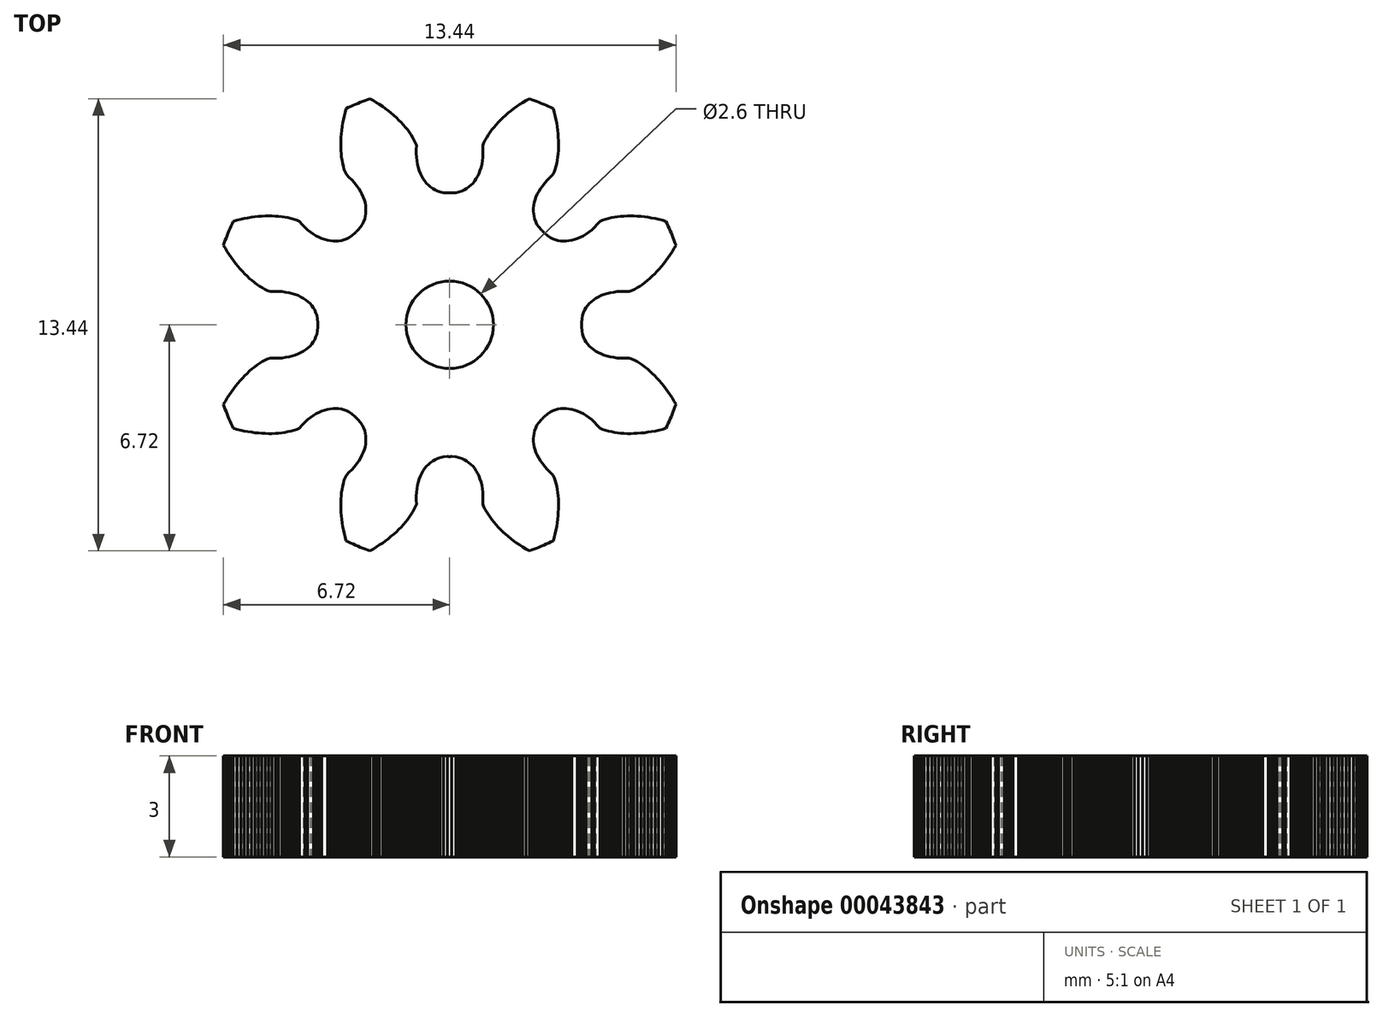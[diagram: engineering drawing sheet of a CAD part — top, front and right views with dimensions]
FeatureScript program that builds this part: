
annotation { "Feature Type Name" : "Feature", "Feature Type Description" : "" }
export const myFeature = defineFeature(function(context is Context, id is Id, definition is map)
    precondition{}
    {
        {
            var Q0;
            Q0=qCreatedBy(makeId("Top.planeOp"),FACE);
            var sketch = newSketch(context, id + "F0", { "sketchPlane" : qUnion([Q0])});
            skLineSegment(sketch, "E0", {"start": v(3.92, 0) * mm, "end": v(3.92, 0.01) * mm});
            skLineSegment(sketch, "E1", {"start": v(3.92, 0.01) * mm, "end": v(3.92, 0.03) * mm});
            skLineSegment(sketch, "E2", {"start": v(3.92, 0.03) * mm, "end": v(3.92, 0.04) * mm});
            skLineSegment(sketch, "E3", {"start": v(3.92, 0.04) * mm, "end": v(3.92, 0.05) * mm});
            skLineSegment(sketch, "E4", {"start": v(3.92, 0.05) * mm, "end": v(3.92, 0.06) * mm});
            skLineSegment(sketch, "E5", {"start": v(3.92, 0.06) * mm, "end": v(3.93, 0.18) * mm});
            skLineSegment(sketch, "E6", {"start": v(3.93, 0.18) * mm, "end": v(3.95, 0.28) * mm});
            skLineSegment(sketch, "E7", {"start": v(3.95, 0.28) * mm, "end": v(3.97, 0.36) * mm});
            skLineSegment(sketch, "E8", {"start": v(3.97, 0.36) * mm, "end": v(4, 0.44) * mm});
            skLineSegment(sketch, "E9", {"start": v(4, 0.44) * mm, "end": v(4.05, 0.5) * mm});
            skLineSegment(sketch, "E10", {"start": v(4.05, 0.5) * mm, "end": v(4.1, 0.57) * mm});
            skLineSegment(sketch, "E11", {"start": v(4.1, 0.57) * mm, "end": v(4.15, 0.63) * mm});
            skLineSegment(sketch, "E12", {"start": v(4.15, 0.63) * mm, "end": v(4.2, 0.69) * mm});
            skLineSegment(sketch, "E13", {"start": v(4.2, 0.69) * mm, "end": v(4.27, 0.74) * mm});
            skLineSegment(sketch, "E14", {"start": v(4.27, 0.74) * mm, "end": v(4.34, 0.79) * mm});
            skLineSegment(sketch, "E15", {"start": v(4.34, 0.79) * mm, "end": v(4.42, 0.83) * mm});
            skLineSegment(sketch, "E16", {"start": v(4.42, 0.83) * mm, "end": v(4.5, 0.87) * mm});
            skLineSegment(sketch, "E17", {"start": v(4.5, 0.87) * mm, "end": v(4.58, 0.9) * mm});
            skLineSegment(sketch, "E18", {"start": v(4.58, 0.9) * mm, "end": v(4.67, 0.93) * mm});
            skLineSegment(sketch, "E19", {"start": v(4.67, 0.93) * mm, "end": v(4.77, 0.96) * mm});
            skLineSegment(sketch, "E20", {"start": v(4.77, 0.96) * mm, "end": v(4.87, 0.97) * mm});
            skLineSegment(sketch, "E21", {"start": v(4.87, 0.97) * mm, "end": v(4.98, 0.99) * mm});
            skLineSegment(sketch, "E22", {"start": v(4.98, 0.99) * mm, "end": v(5.1, 1) * mm});
            skLineSegment(sketch, "E23", {"start": v(5.1, 1) * mm, "end": v(5.2, 0.99) * mm});
            skLineSegment(sketch, "E24", {"start": v(5.2, 0.99) * mm, "end": v(5.33, 0.99) * mm});
            skLineSegment(sketch, "E25", {"start": v(5.33, 0.99) * mm, "end": v(5.41, 1.02) * mm});
            skLineSegment(sketch, "E26", {"start": v(5.41, 1.02) * mm, "end": v(5.49, 1.06) * mm});
            skLineSegment(sketch, "E27", {"start": v(5.49, 1.06) * mm, "end": v(5.57, 1.1) * mm});
            skLineSegment(sketch, "E28", {"start": v(5.57, 1.1) * mm, "end": v(5.65, 1.15) * mm});
            skLineSegment(sketch, "E29", {"start": v(5.65, 1.15) * mm, "end": v(5.72, 1.2) * mm});
            skLineSegment(sketch, "E30", {"start": v(5.72, 1.2) * mm, "end": v(5.8, 1.25) * mm});
            skLineSegment(sketch, "E31", {"start": v(5.8, 1.25) * mm, "end": v(5.87, 1.31) * mm});
            skLineSegment(sketch, "E32", {"start": v(5.87, 1.31) * mm, "end": v(5.94, 1.38) * mm});
            skLineSegment(sketch, "E33", {"start": v(5.94, 1.38) * mm, "end": v(6.02, 1.44) * mm});
            skLineSegment(sketch, "E34", {"start": v(6.02, 1.44) * mm, "end": v(6.09, 1.51) * mm});
            skLineSegment(sketch, "E35", {"start": v(6.09, 1.51) * mm, "end": v(6.16, 1.58) * mm});
            skLineSegment(sketch, "E36", {"start": v(6.16, 1.58) * mm, "end": v(6.23, 1.66) * mm});
            skLineSegment(sketch, "E37", {"start": v(6.23, 1.66) * mm, "end": v(6.3, 1.74) * mm});
            skLineSegment(sketch, "E38", {"start": v(6.3, 1.74) * mm, "end": v(6.36, 1.82) * mm});
            skLineSegment(sketch, "E39", {"start": v(6.36, 1.82) * mm, "end": v(6.42, 1.9) * mm});
            skLineSegment(sketch, "E40", {"start": v(6.42, 1.9) * mm, "end": v(6.48, 2) * mm});
            skLineSegment(sketch, "E41", {"start": v(6.48, 2) * mm, "end": v(6.55, 2.08) * mm});
            skLineSegment(sketch, "E42", {"start": v(6.55, 2.08) * mm, "end": v(6.6, 2.17) * mm});
            skLineSegment(sketch, "E43", {"start": v(6.6, 2.17) * mm, "end": v(6.66, 2.27) * mm});
            skLineSegment(sketch, "E44", {"start": v(6.66, 2.27) * mm, "end": v(6.72, 2.37) * mm});
            skLineSegment(sketch, "E45", {"start": v(6.72, 2.37) * mm, "end": v(6.7, 2.44) * mm});
            skLineSegment(sketch, "E46", {"start": v(6.7, 2.44) * mm, "end": v(6.67, 2.51) * mm});
            skLineSegment(sketch, "E47", {"start": v(6.67, 2.51) * mm, "end": v(6.64, 2.58) * mm});
            skLineSegment(sketch, "E48", {"start": v(6.64, 2.58) * mm, "end": v(6.61, 2.66) * mm});
            skLineSegment(sketch, "E49", {"start": v(6.61, 2.66) * mm, "end": v(6.58, 2.73) * mm});
            skPoint(sketch, "E50", {"position": v(0, 5.7) * mm});
            skPoint(sketch, "E51", {"position": v(5.7, 0) * mm});
            skPoint(sketch, "E52", {"position": v(0, 0) * mm});
            skPoint(sketch, "E53", {"position": v(0, -5.7) * mm});
            skCircle(sketch, "E54", {"center": v(0, 0) * mm, "radius": 5.7 * mm, "construction": true});
            skLineSegment(sketch, "E55", {"start": v(5.7, 0) * mm, "end": v(-5.7, 0) * mm, "construction": true});
            skLineSegment(sketch, "E56", {"start": v(0, 5.7) * mm, "end": v(0, -5.7) * mm, "construction": true});
            skLineSegment(sketch, "E57.MirrorCS", {"start": v(3.92, 0) * mm, "end": v(3.92, -0.01) * mm});
            skLineSegment(sketch, "E58.MirrorCS", {"start": v(3.92, -0.03) * mm, "end": v(3.92, -0.04) * mm});
            skLineSegment(sketch, "E59.MirrorCS", {"start": v(3.92, -0.05) * mm, "end": v(3.92, -0.06) * mm});
            skLineSegment(sketch, "E60.MirrorCS", {"start": v(3.92, -0.01) * mm, "end": v(3.92, -0.03) * mm});
            skLineSegment(sketch, "E61.MirrorCS", {"start": v(3.92, -0.04) * mm, "end": v(3.92, -0.05) * mm});
            skLineSegment(sketch, "E62.MirrorCS", {"start": v(6.09, -1.51) * mm, "end": v(6.16, -1.58) * mm});
            skLineSegment(sketch, "E63.MirrorCS", {"start": v(4.67, -0.93) * mm, "end": v(4.77, -0.96) * mm});
            skLineSegment(sketch, "E64.MirrorCS", {"start": v(4.2, -0.69) * mm, "end": v(4.27, -0.74) * mm});
            skLineSegment(sketch, "E65.MirrorCS", {"start": v(4.27, -0.74) * mm, "end": v(4.34, -0.79) * mm});
            skLineSegment(sketch, "E66.MirrorCS", {"start": v(4.34, -0.79) * mm, "end": v(4.42, -0.83) * mm});
            skLineSegment(sketch, "E67.MirrorCS", {"start": v(3.92, -0.06) * mm, "end": v(3.93, -0.18) * mm});
            skLineSegment(sketch, "E68.MirrorCS", {"start": v(3.93, -0.18) * mm, "end": v(3.95, -0.28) * mm});
            skLineSegment(sketch, "E69.MirrorCS", {"start": v(3.95, -0.28) * mm, "end": v(3.97, -0.36) * mm});
            skLineSegment(sketch, "E70.MirrorCS", {"start": v(6.02, -1.44) * mm, "end": v(6.09, -1.51) * mm});
            skLineSegment(sketch, "E71.MirrorCS", {"start": v(3.97, -0.36) * mm, "end": v(4, -0.44) * mm});
            skLineSegment(sketch, "E72.MirrorCS", {"start": v(4, -0.44) * mm, "end": v(4.05, -0.5) * mm});
            skLineSegment(sketch, "E73.MirrorCS", {"start": v(4.05, -0.5) * mm, "end": v(4.1, -0.57) * mm});
            skLineSegment(sketch, "E74.MirrorCS", {"start": v(4.1, -0.57) * mm, "end": v(4.15, -0.63) * mm});
            skLineSegment(sketch, "E75.MirrorCS", {"start": v(4.15, -0.63) * mm, "end": v(4.2, -0.69) * mm});
            skLineSegment(sketch, "E76.MirrorCS", {"start": v(5.49, -1.06) * mm, "end": v(5.57, -1.1) * mm});
            skLineSegment(sketch, "E77.MirrorCS", {"start": v(6.6, -2.17) * mm, "end": v(6.66, -2.27) * mm});
            skLineSegment(sketch, "E78.MirrorCS", {"start": v(6.36, -1.82) * mm, "end": v(6.42, -1.9) * mm});
            skLineSegment(sketch, "E79.MirrorCS", {"start": v(5.1, -1) * mm, "end": v(5.2, -0.99) * mm});
            skLineSegment(sketch, "E80.MirrorCS", {"start": v(4.77, -0.96) * mm, "end": v(4.87, -0.97) * mm});
            skLineSegment(sketch, "E81.MirrorCS", {"start": v(6.72, -2.37) * mm, "end": v(6.7, -2.44) * mm});
            skLineSegment(sketch, "E82.MirrorCS", {"start": v(5.41, -1.02) * mm, "end": v(5.49, -1.06) * mm});
            skLineSegment(sketch, "E83.MirrorCS", {"start": v(5.65, -1.15) * mm, "end": v(5.72, -1.2) * mm});
            skLineSegment(sketch, "E84.MirrorCS", {"start": v(6.16, -1.58) * mm, "end": v(6.23, -1.66) * mm});
            skLineSegment(sketch, "E85.MirrorCS", {"start": v(4.42, -0.83) * mm, "end": v(4.5, -0.87) * mm});
            skLineSegment(sketch, "E86.MirrorCS", {"start": v(6.55, -2.08) * mm, "end": v(6.6, -2.17) * mm});
            skLineSegment(sketch, "E87.MirrorCS", {"start": v(6.64, -2.58) * mm, "end": v(6.61, -2.66) * mm});
            skLineSegment(sketch, "E88.MirrorCS", {"start": v(5.87, -1.31) * mm, "end": v(5.94, -1.38) * mm});
            skLineSegment(sketch, "E89.MirrorCS", {"start": v(6.66, -2.27) * mm, "end": v(6.72, -2.37) * mm});
            skLineSegment(sketch, "E90.MirrorCS", {"start": v(5.57, -1.1) * mm, "end": v(5.65, -1.15) * mm});
            skLineSegment(sketch, "E91.MirrorCS", {"start": v(6.42, -1.9) * mm, "end": v(6.48, -2) * mm});
            skLineSegment(sketch, "E92.MirrorCS", {"start": v(5.2, -0.99) * mm, "end": v(5.33, -0.99) * mm});
            skLineSegment(sketch, "E93.MirrorCS", {"start": v(4.87, -0.97) * mm, "end": v(4.98, -0.99) * mm});
            skLineSegment(sketch, "E94.MirrorCS", {"start": v(6.7, -2.44) * mm, "end": v(6.67, -2.51) * mm});
            skLineSegment(sketch, "E95.MirrorCS", {"start": v(5.72, -1.2) * mm, "end": v(5.8, -1.25) * mm});
            skLineSegment(sketch, "E96.MirrorCS", {"start": v(4.58, -0.9) * mm, "end": v(4.67, -0.93) * mm});
            skLineSegment(sketch, "E97.MirrorCS", {"start": v(6.23, -1.66) * mm, "end": v(6.3, -1.74) * mm});
            skLineSegment(sketch, "E98.MirrorCS", {"start": v(4.5, -0.87) * mm, "end": v(4.58, -0.9) * mm});
            skLineSegment(sketch, "E99.MirrorCS", {"start": v(6.61, -2.66) * mm, "end": v(6.58, -2.73) * mm});
            skLineSegment(sketch, "E100.MirrorCS", {"start": v(5.94, -1.38) * mm, "end": v(6.02, -1.44) * mm});
            skLineSegment(sketch, "E101.MirrorCS", {"start": v(6.48, -2) * mm, "end": v(6.55, -2.08) * mm});
            skLineSegment(sketch, "E102.MirrorCS", {"start": v(5.33, -0.99) * mm, "end": v(5.41, -1.02) * mm});
            skLineSegment(sketch, "E103.MirrorCS", {"start": v(6.67, -2.51) * mm, "end": v(6.64, -2.58) * mm});
            skLineSegment(sketch, "E104.MirrorCS", {"start": v(4.98, -0.99) * mm, "end": v(5.1, -1) * mm});
            skLineSegment(sketch, "E105.MirrorCS", {"start": v(6.3, -1.74) * mm, "end": v(6.36, -1.82) * mm});
            skLineSegment(sketch, "E106.MirrorCS", {"start": v(5.8, -1.25) * mm, "end": v(5.87, -1.31) * mm});
            skPoint(sketch, "E107.1.0", {"position": v(4.03, 4.03) * mm});
            skPoint(sketch, "E107.1.1", {"position": v(4.03, 4.03) * mm});
            skLineSegment(sketch, "E107.1.2", {"start": v(4.22, 2.82) * mm, "end": v(4.3, 2.9) * mm});
            skLineSegment(sketch, "E107.1.3", {"start": v(5.58, 3.23) * mm, "end": v(5.68, 3.22) * mm});
            skLineSegment(sketch, "E107.1.4", {"start": v(5.37, 3.23) * mm, "end": v(5.47, 3.23) * mm});
            skLineSegment(sketch, "E107.1.5", {"start": v(3.16, 6.1) * mm, "end": v(3.13, 6.2) * mm});
            skLineSegment(sketch, "E107.1.6", {"start": v(3.1, 4.54) * mm, "end": v(3.14, 4.63) * mm});
            skLineSegment(sketch, "E107.1.7", {"start": v(5.78, 3.2) * mm, "end": v(5.89, 3.2) * mm});
            skLineSegment(sketch, "E107.1.8", {"start": v(2.65, 3.96) * mm, "end": v(2.7, 4.05) * mm});
            skLineSegment(sketch, "E107.1.9", {"start": v(3.06, 2.56) * mm, "end": v(3.15, 2.52) * mm});
            skLineSegment(sketch, "E107.1.10", {"start": v(4.8, 3.18) * mm, "end": v(4.9, 3.2) * mm});
            skLineSegment(sketch, "E107.1.11", {"start": v(3.23, 5.37) * mm, "end": v(3.23, 5.47) * mm});
            skLineSegment(sketch, "E107.1.12", {"start": v(3.1, 6.32) * mm, "end": v(3.08, 6.43) * mm});
            skLineSegment(sketch, "E107.1.13", {"start": v(3.46, 2.49) * mm, "end": v(3.54, 2.5) * mm});
            skLineSegment(sketch, "E107.1.14", {"start": v(3.16, 4.71) * mm, "end": v(3.18, 4.8) * mm});
            skLineSegment(sketch, "E107.1.15", {"start": v(4.05, 2.7) * mm, "end": v(4.13, 2.76) * mm});
            skLineSegment(sketch, "E107.1.16", {"start": v(3.88, 2.6) * mm, "end": v(3.96, 2.65) * mm});
            skLineSegment(sketch, "E107.1.17", {"start": v(4.54, 3.1) * mm, "end": v(4.63, 3.14) * mm});
            skLineSegment(sketch, "E107.1.18", {"start": v(3.63, 2.51) * mm, "end": v(3.71, 2.54) * mm});
            skLineSegment(sketch, "E107.1.19", {"start": v(6.32, 3.1) * mm, "end": v(6.43, 3.08) * mm});
            skLineSegment(sketch, "E107.1.20", {"start": v(3.22, 2.5) * mm, "end": v(3.3, 2.5) * mm});
            skLineSegment(sketch, "E107.1.21", {"start": v(3.23, 5.58) * mm, "end": v(3.22, 5.68) * mm});
            skLineSegment(sketch, "E107.1.22", {"start": v(3.2, 4.9) * mm, "end": v(3.21, 4.99) * mm});
            skLineSegment(sketch, "E107.1.23", {"start": v(4.71, 3.16) * mm, "end": v(4.8, 3.18) * mm});
            skLineSegment(sketch, "E107.1.24", {"start": v(3.96, 2.65) * mm, "end": v(4.05, 2.7) * mm});
            skLineSegment(sketch, "E107.1.25", {"start": v(3.13, 6.2) * mm, "end": v(3.1, 6.32) * mm});
            skLineSegment(sketch, "E107.1.26", {"start": v(4.9, 3.2) * mm, "end": v(4.99, 3.21) * mm});
            skLineSegment(sketch, "E107.1.27", {"start": v(3.14, 4.63) * mm, "end": v(3.16, 4.71) * mm});
            skLineSegment(sketch, "E107.1.28", {"start": v(2.7, 4.05) * mm, "end": v(2.76, 4.13) * mm});
            skLineSegment(sketch, "E107.1.29", {"start": v(4.3, 2.9) * mm, "end": v(4.38, 2.98) * mm});
            skLineSegment(sketch, "E107.1.30", {"start": v(5.08, 3.22) * mm, "end": v(5.18, 3.23) * mm});
            skLineSegment(sketch, "E107.1.31", {"start": v(5.68, 3.22) * mm, "end": v(5.78, 3.2) * mm});
            skLineSegment(sketch, "E107.1.32", {"start": v(3.8, 2.57) * mm, "end": v(3.88, 2.6) * mm});
            skLineSegment(sketch, "E107.1.33", {"start": v(3.15, 2.52) * mm, "end": v(3.22, 2.5) * mm});
            skLineSegment(sketch, "E107.1.34", {"start": v(3.54, 2.5) * mm, "end": v(3.63, 2.51) * mm});
            skLineSegment(sketch, "E107.1.35", {"start": v(3.23, 5.47) * mm, "end": v(3.23, 5.58) * mm});
            skLineSegment(sketch, "E107.1.36", {"start": v(3.18, 4.8) * mm, "end": v(3.2, 4.9) * mm});
            skLineSegment(sketch, "E107.1.37", {"start": v(3.3, 2.5) * mm, "end": v(3.38, 2.49) * mm});
            skLineSegment(sketch, "E107.1.38", {"start": v(3.22, 5.68) * mm, "end": v(3.2, 5.78) * mm});
            skLineSegment(sketch, "E107.1.39", {"start": v(3.21, 4.99) * mm, "end": v(3.22, 5.08) * mm});
            skLineSegment(sketch, "E107.1.40", {"start": v(4.99, 3.21) * mm, "end": v(5.08, 3.22) * mm});
            skLineSegment(sketch, "E107.1.41", {"start": v(6.55, 2.8) * mm, "end": v(6.58, 2.73) * mm});
            skLineSegment(sketch, "E107.1.42", {"start": v(2.49, 3.46) * mm, "end": v(2.5, 3.54) * mm});
            skLineSegment(sketch, "E107.1.43", {"start": v(2.5, 3.54) * mm, "end": v(2.51, 3.63) * mm});
            skLineSegment(sketch, "E107.1.44", {"start": v(2.51, 3.63) * mm, "end": v(2.54, 3.71) * mm});
            skLineSegment(sketch, "E107.1.45", {"start": v(2.65, 2.9) * mm, "end": v(2.6, 2.99) * mm});
            skLineSegment(sketch, "E107.1.46", {"start": v(2.6, 2.99) * mm, "end": v(2.56, 3.06) * mm});
            skLineSegment(sketch, "E107.1.47", {"start": v(2.56, 3.06) * mm, "end": v(2.52, 3.15) * mm});
            skLineSegment(sketch, "E107.1.48", {"start": v(2.52, 3.15) * mm, "end": v(2.5, 3.22) * mm});
            skLineSegment(sketch, "E107.1.49", {"start": v(2.5, 3.22) * mm, "end": v(2.5, 3.3) * mm});
            skLineSegment(sketch, "E107.1.50", {"start": v(2.5, 3.3) * mm, "end": v(2.49, 3.38) * mm});
            skLineSegment(sketch, "E107.1.51", {"start": v(2.49, 3.38) * mm, "end": v(2.49, 3.46) * mm});
            skLineSegment(sketch, "E107.1.52", {"start": v(5.18, 3.23) * mm, "end": v(5.27, 3.23) * mm});
            skLineSegment(sketch, "E107.1.53", {"start": v(3.2, 5.78) * mm, "end": v(3.2, 5.89) * mm});
            skLineSegment(sketch, "E107.1.54", {"start": v(5.89, 3.2) * mm, "end": v(6, 3.18) * mm});
            skLineSegment(sketch, "E107.1.55", {"start": v(3.38, 2.49) * mm, "end": v(3.46, 2.49) * mm});
            skLineSegment(sketch, "E107.1.56", {"start": v(2.54, 3.71) * mm, "end": v(2.57, 3.8) * mm});
            skLineSegment(sketch, "E107.1.57", {"start": v(5.47, 3.23) * mm, "end": v(5.58, 3.23) * mm});
            skLineSegment(sketch, "E107.1.58", {"start": v(3.22, 5.08) * mm, "end": v(3.23, 5.18) * mm});
            skLineSegment(sketch, "E107.1.59", {"start": v(3.2, 5.89) * mm, "end": v(3.18, 6) * mm});
            skLineSegment(sketch, "E107.1.60", {"start": v(2.98, 4.38) * mm, "end": v(3.07, 4.47) * mm});
            skLineSegment(sketch, "E107.1.61", {"start": v(4.38, 2.98) * mm, "end": v(4.47, 3.07) * mm});
            skLineSegment(sketch, "E107.1.62", {"start": v(4.63, 3.14) * mm, "end": v(4.71, 3.16) * mm});
            skLineSegment(sketch, "E107.1.63", {"start": v(2.57, 3.8) * mm, "end": v(2.6, 3.88) * mm});
            skLineSegment(sketch, "E107.1.64", {"start": v(3.71, 2.54) * mm, "end": v(3.8, 2.57) * mm});
            skLineSegment(sketch, "E107.1.65", {"start": v(3.23, 5.18) * mm, "end": v(3.23, 5.27) * mm});
            skLineSegment(sketch, "E107.1.66", {"start": v(6, 3.18) * mm, "end": v(6.1, 3.16) * mm});
            skLineSegment(sketch, "E107.1.67", {"start": v(3.18, 6) * mm, "end": v(3.16, 6.1) * mm});
            skLineSegment(sketch, "E107.1.68", {"start": v(3.07, 4.47) * mm, "end": v(3.1, 4.54) * mm});
            skLineSegment(sketch, "E107.1.69", {"start": v(4.13, 2.76) * mm, "end": v(4.22, 2.82) * mm});
            skLineSegment(sketch, "E107.1.70", {"start": v(6.2, 3.13) * mm, "end": v(6.32, 3.1) * mm});
            skLineSegment(sketch, "E107.1.71", {"start": v(2.6, 3.88) * mm, "end": v(2.65, 3.96) * mm});
            skLineSegment(sketch, "E107.1.72", {"start": v(6.1, 3.16) * mm, "end": v(6.2, 3.13) * mm});
            skLineSegment(sketch, "E107.1.73", {"start": v(5.27, 3.23) * mm, "end": v(5.37, 3.23) * mm});
            skLineSegment(sketch, "E107.1.74", {"start": v(3.23, 5.27) * mm, "end": v(3.23, 5.37) * mm});
            skLineSegment(sketch, "E107.1.75", {"start": v(4.47, 3.07) * mm, "end": v(4.54, 3.1) * mm});
            skLineSegment(sketch, "E107.1.76", {"start": v(2.76, 4.13) * mm, "end": v(2.82, 4.22) * mm});
            skLineSegment(sketch, "E107.1.77", {"start": v(2.82, 4.22) * mm, "end": v(2.9, 4.3) * mm});
            skLineSegment(sketch, "E107.1.78", {"start": v(2.9, 4.3) * mm, "end": v(2.98, 4.38) * mm});
            skLineSegment(sketch, "E107.1.79", {"start": v(2.8, 6.55) * mm, "end": v(2.73, 6.58) * mm});
            skLineSegment(sketch, "E107.1.80", {"start": v(6.46, 3) * mm, "end": v(6.5, 2.94) * mm});
            skLineSegment(sketch, "E107.1.81", {"start": v(6.52, 2.87) * mm, "end": v(6.55, 2.8) * mm});
            skLineSegment(sketch, "E107.1.82", {"start": v(6.5, 2.94) * mm, "end": v(6.52, 2.87) * mm});
            skLineSegment(sketch, "E107.1.83", {"start": v(3, 6.46) * mm, "end": v(2.94, 6.5) * mm});
            skLineSegment(sketch, "E107.1.84", {"start": v(6.43, 3.08) * mm, "end": v(6.46, 3) * mm});
            skLineSegment(sketch, "E107.1.85", {"start": v(3.08, 6.43) * mm, "end": v(3, 6.46) * mm});
            skLineSegment(sketch, "E107.1.86", {"start": v(2.94, 6.5) * mm, "end": v(2.87, 6.52) * mm});
            skLineSegment(sketch, "E107.1.87", {"start": v(2.9, 2.65) * mm, "end": v(2.99, 2.6) * mm});
            skLineSegment(sketch, "E107.1.88", {"start": v(2.87, 6.52) * mm, "end": v(2.8, 6.55) * mm});
            skLineSegment(sketch, "E107.1.89", {"start": v(2.99, 2.6) * mm, "end": v(3.06, 2.56) * mm});
            skLineSegment(sketch, "E107.1.90", {"start": v(2.82, 2.73) * mm, "end": v(2.9, 2.65) * mm});
            skLineSegment(sketch, "E107.1.91", {"start": v(2.79, 2.75) * mm, "end": v(2.8, 2.74) * mm});
            skLineSegment(sketch, "E107.1.92", {"start": v(2.76, 2.78) * mm, "end": v(2.75, 2.79) * mm});
            skLineSegment(sketch, "E107.1.93", {"start": v(2.73, 2.82) * mm, "end": v(2.65, 2.9) * mm});
            skLineSegment(sketch, "E107.1.94", {"start": v(2.74, 2.8) * mm, "end": v(2.73, 2.82) * mm});
            skLineSegment(sketch, "E107.1.95", {"start": v(2.74, 2.8) * mm, "end": v(2.74, 2.8) * mm});
            skLineSegment(sketch, "E107.1.96", {"start": v(2.75, 2.79) * mm, "end": v(2.74, 2.8) * mm});
            skLineSegment(sketch, "E107.1.97", {"start": v(2.77, 2.77) * mm, "end": v(2.76, 2.78) * mm});
            skLineSegment(sketch, "E107.1.98", {"start": v(2.77, 2.77) * mm, "end": v(2.78, 2.76) * mm});
            skLineSegment(sketch, "E107.1.99", {"start": v(2.78, 2.76) * mm, "end": v(2.79, 2.75) * mm});
            skLineSegment(sketch, "E107.1.100", {"start": v(2.8, 2.74) * mm, "end": v(2.8, 2.74) * mm});
            skLineSegment(sketch, "E107.1.101", {"start": v(2.8, 2.74) * mm, "end": v(2.82, 2.73) * mm});
            skLineSegment(sketch, "E107.2.2", {"start": v(0.99, 4.98) * mm, "end": v(1, 5.1) * mm});
            skLineSegment(sketch, "E107.2.3", {"start": v(1.66, 6.23) * mm, "end": v(1.74, 6.3) * mm});
            skLineSegment(sketch, "E107.2.4", {"start": v(1.51, 6.09) * mm, "end": v(1.58, 6.16) * mm});
            skLineSegment(sketch, "E107.2.5", {"start": v(-2.08, 6.55) * mm, "end": v(-2.17, 6.6) * mm});
            skLineSegment(sketch, "E107.2.6", {"start": v(-1.02, 5.41) * mm, "end": v(-1.06, 5.49) * mm});
            skLineSegment(sketch, "E107.2.7", {"start": v(1.82, 6.36) * mm, "end": v(1.9, 6.42) * mm});
            skLineSegment(sketch, "E107.2.8", {"start": v(-0.93, 4.67) * mm, "end": v(-0.96, 4.77) * mm});
            skLineSegment(sketch, "E107.2.9", {"start": v(0.36, 3.97) * mm, "end": v(0.44, 4) * mm});
            skLineSegment(sketch, "E107.2.10", {"start": v(1.15, 5.65) * mm, "end": v(1.2, 5.72) * mm});
            skLineSegment(sketch, "E107.2.11", {"start": v(-1.51, 6.09) * mm, "end": v(-1.58, 6.16) * mm});
            skLineSegment(sketch, "E107.2.12", {"start": v(-2.27, 6.66) * mm, "end": v(-2.37, 6.72) * mm});
            skLineSegment(sketch, "E107.2.13", {"start": v(0.69, 4.2) * mm, "end": v(0.74, 4.27) * mm});
            skLineSegment(sketch, "E107.2.14", {"start": v(-1.1, 5.57) * mm, "end": v(-1.15, 5.65) * mm});
            skLineSegment(sketch, "E107.2.15", {"start": v(0.96, 4.77) * mm, "end": v(0.97, 4.87) * mm});
            skLineSegment(sketch, "E107.2.16", {"start": v(0.9, 4.58) * mm, "end": v(0.93, 4.67) * mm});
            skLineSegment(sketch, "E107.2.17", {"start": v(1.02, 5.41) * mm, "end": v(1.06, 5.49) * mm});
            skLineSegment(sketch, "E107.2.18", {"start": v(0.79, 4.34) * mm, "end": v(0.83, 4.42) * mm});
            skLineSegment(sketch, "E107.2.19", {"start": v(2.27, 6.66) * mm, "end": v(2.37, 6.72) * mm});
            skLineSegment(sketch, "E107.2.20", {"start": v(0.5, 4.05) * mm, "end": v(0.57, 4.1) * mm});
            skLineSegment(sketch, "E107.2.21", {"start": v(-1.66, 6.23) * mm, "end": v(-1.74, 6.3) * mm});
            skLineSegment(sketch, "E107.2.22", {"start": v(-1.2, 5.72) * mm, "end": v(-1.25, 5.8) * mm});
            skLineSegment(sketch, "E107.2.23", {"start": v(1.1, 5.57) * mm, "end": v(1.15, 5.65) * mm});
            skLineSegment(sketch, "E107.2.24", {"start": v(0.93, 4.67) * mm, "end": v(0.96, 4.77) * mm});
            skLineSegment(sketch, "E107.2.25", {"start": v(-2.17, 6.6) * mm, "end": v(-2.27, 6.66) * mm});
            skLineSegment(sketch, "E107.2.26", {"start": v(1.2, 5.72) * mm, "end": v(1.25, 5.8) * mm});
            skLineSegment(sketch, "E107.2.27", {"start": v(-1.06, 5.49) * mm, "end": v(-1.1, 5.57) * mm});
            skLineSegment(sketch, "E107.2.28", {"start": v(-0.96, 4.77) * mm, "end": v(-0.97, 4.87) * mm});
            skLineSegment(sketch, "E107.2.29", {"start": v(1, 5.1) * mm, "end": v(0.99, 5.2) * mm});
            skLineSegment(sketch, "E107.2.30", {"start": v(1.31, 5.87) * mm, "end": v(1.38, 5.94) * mm});
            skLineSegment(sketch, "E107.2.31", {"start": v(1.74, 6.3) * mm, "end": v(1.82, 6.36) * mm});
            skLineSegment(sketch, "E107.2.32", {"start": v(0.87, 4.5) * mm, "end": v(0.9, 4.58) * mm});
            skLineSegment(sketch, "E107.2.33", {"start": v(0.44, 4) * mm, "end": v(0.5, 4.05) * mm});
            skLineSegment(sketch, "E107.2.34", {"start": v(0.74, 4.27) * mm, "end": v(0.79, 4.34) * mm});
            skLineSegment(sketch, "E107.2.35", {"start": v(-1.58, 6.16) * mm, "end": v(-1.66, 6.23) * mm});
            skLineSegment(sketch, "E107.2.36", {"start": v(-1.15, 5.65) * mm, "end": v(-1.2, 5.72) * mm});
            skLineSegment(sketch, "E107.2.37", {"start": v(0.57, 4.1) * mm, "end": v(0.63, 4.15) * mm});
            skLineSegment(sketch, "E107.2.38", {"start": v(-1.74, 6.3) * mm, "end": v(-1.82, 6.36) * mm});
            skLineSegment(sketch, "E107.2.39", {"start": v(-1.25, 5.8) * mm, "end": v(-1.31, 5.87) * mm});
            skLineSegment(sketch, "E107.2.40", {"start": v(1.25, 5.8) * mm, "end": v(1.31, 5.87) * mm});
            skLineSegment(sketch, "E107.2.41", {"start": v(2.66, 6.61) * mm, "end": v(2.73, 6.58) * mm});
            skLineSegment(sketch, "E107.2.42", {"start": v(-0.69, 4.2) * mm, "end": v(-0.74, 4.27) * mm});
            skLineSegment(sketch, "E107.2.43", {"start": v(-0.74, 4.27) * mm, "end": v(-0.79, 4.34) * mm});
            skLineSegment(sketch, "E107.2.44", {"start": v(-0.79, 4.34) * mm, "end": v(-0.83, 4.42) * mm});
            skLineSegment(sketch, "E107.2.45", {"start": v(-0.18, 3.93) * mm, "end": v(-0.28, 3.95) * mm});
            skLineSegment(sketch, "E107.2.46", {"start": v(-0.28, 3.95) * mm, "end": v(-0.36, 3.97) * mm});
            skLineSegment(sketch, "E107.2.47", {"start": v(-0.36, 3.97) * mm, "end": v(-0.44, 4) * mm});
            skLineSegment(sketch, "E107.2.48", {"start": v(-0.44, 4) * mm, "end": v(-0.5, 4.05) * mm});
            skLineSegment(sketch, "E107.2.49", {"start": v(-0.5, 4.05) * mm, "end": v(-0.57, 4.1) * mm});
            skLineSegment(sketch, "E107.2.50", {"start": v(-0.57, 4.1) * mm, "end": v(-0.63, 4.15) * mm});
            skLineSegment(sketch, "E107.2.51", {"start": v(-0.63, 4.15) * mm, "end": v(-0.69, 4.2) * mm});
            skLineSegment(sketch, "E107.2.52", {"start": v(1.38, 5.94) * mm, "end": v(1.44, 6.02) * mm});
            skLineSegment(sketch, "E107.2.53", {"start": v(-1.82, 6.36) * mm, "end": v(-1.9, 6.42) * mm});
            skLineSegment(sketch, "E107.2.54", {"start": v(1.9, 6.42) * mm, "end": v(2, 6.48) * mm});
            skLineSegment(sketch, "E107.2.55", {"start": v(0.63, 4.15) * mm, "end": v(0.69, 4.2) * mm});
            skLineSegment(sketch, "E107.2.56", {"start": v(-0.83, 4.42) * mm, "end": v(-0.87, 4.5) * mm});
            skLineSegment(sketch, "E107.2.57", {"start": v(1.58, 6.16) * mm, "end": v(1.66, 6.23) * mm});
            skLineSegment(sketch, "E107.2.58", {"start": v(-1.31, 5.87) * mm, "end": v(-1.38, 5.94) * mm});
            skLineSegment(sketch, "E107.2.59", {"start": v(-1.9, 6.42) * mm, "end": v(-2, 6.48) * mm});
            skLineSegment(sketch, "E107.2.60", {"start": v(-0.99, 5.2) * mm, "end": v(-0.99, 5.33) * mm});
            skLineSegment(sketch, "E107.2.61", {"start": v(0.99, 5.2) * mm, "end": v(0.99, 5.33) * mm});
            skLineSegment(sketch, "E107.2.62", {"start": v(1.06, 5.49) * mm, "end": v(1.1, 5.57) * mm});
            skLineSegment(sketch, "E107.2.63", {"start": v(-0.87, 4.5) * mm, "end": v(-0.9, 4.58) * mm});
            skLineSegment(sketch, "E107.2.64", {"start": v(0.83, 4.42) * mm, "end": v(0.87, 4.5) * mm});
            skLineSegment(sketch, "E107.2.65", {"start": v(-1.38, 5.94) * mm, "end": v(-1.44, 6.02) * mm});
            skLineSegment(sketch, "E107.2.66", {"start": v(2, 6.48) * mm, "end": v(2.08, 6.55) * mm});
            skLineSegment(sketch, "E107.2.67", {"start": v(-2, 6.48) * mm, "end": v(-2.08, 6.55) * mm});
            skLineSegment(sketch, "E107.2.68", {"start": v(-0.99, 5.33) * mm, "end": v(-1.02, 5.41) * mm});
            skLineSegment(sketch, "E107.2.69", {"start": v(0.97, 4.87) * mm, "end": v(0.99, 4.98) * mm});
            skLineSegment(sketch, "E107.2.70", {"start": v(2.17, 6.6) * mm, "end": v(2.27, 6.66) * mm});
            skLineSegment(sketch, "E107.2.71", {"start": v(-0.9, 4.58) * mm, "end": v(-0.93, 4.67) * mm});
            skLineSegment(sketch, "E107.2.72", {"start": v(2.08, 6.55) * mm, "end": v(2.17, 6.6) * mm});
            skLineSegment(sketch, "E107.2.73", {"start": v(1.44, 6.02) * mm, "end": v(1.51, 6.09) * mm});
            skLineSegment(sketch, "E107.2.74", {"start": v(-1.44, 6.02) * mm, "end": v(-1.51, 6.09) * mm});
            skLineSegment(sketch, "E107.2.75", {"start": v(0.99, 5.33) * mm, "end": v(1.02, 5.41) * mm});
            skLineSegment(sketch, "E107.2.76", {"start": v(-0.97, 4.87) * mm, "end": v(-0.99, 4.98) * mm});
            skLineSegment(sketch, "E107.2.77", {"start": v(-0.99, 4.98) * mm, "end": v(-1, 5.1) * mm});
            skLineSegment(sketch, "E107.2.78", {"start": v(-1, 5.1) * mm, "end": v(-0.99, 5.2) * mm});
            skLineSegment(sketch, "E107.2.79", {"start": v(-2.66, 6.61) * mm, "end": v(-2.73, 6.58) * mm});
            skLineSegment(sketch, "E107.2.80", {"start": v(2.44, 6.7) * mm, "end": v(2.51, 6.67) * mm});
            skLineSegment(sketch, "E107.2.81", {"start": v(2.58, 6.64) * mm, "end": v(2.66, 6.61) * mm});
            skLineSegment(sketch, "E107.2.82", {"start": v(2.51, 6.67) * mm, "end": v(2.58, 6.64) * mm});
            skLineSegment(sketch, "E107.2.83", {"start": v(-2.44, 6.7) * mm, "end": v(-2.51, 6.67) * mm});
            skLineSegment(sketch, "E107.2.84", {"start": v(2.37, 6.72) * mm, "end": v(2.44, 6.7) * mm});
            skLineSegment(sketch, "E107.2.85", {"start": v(-2.37, 6.72) * mm, "end": v(-2.44, 6.7) * mm});
            skLineSegment(sketch, "E107.2.86", {"start": v(-2.51, 6.67) * mm, "end": v(-2.58, 6.64) * mm});
            skLineSegment(sketch, "E107.2.87", {"start": v(0.18, 3.93) * mm, "end": v(0.28, 3.95) * mm});
            skLineSegment(sketch, "E107.2.88", {"start": v(-2.58, 6.64) * mm, "end": v(-2.66, 6.61) * mm});
            skLineSegment(sketch, "E107.2.89", {"start": v(0.28, 3.95) * mm, "end": v(0.36, 3.97) * mm});
            skLineSegment(sketch, "E107.2.90", {"start": v(0.06, 3.92) * mm, "end": v(0.18, 3.93) * mm});
            skLineSegment(sketch, "E107.2.91", {"start": v(0.03, 3.92) * mm, "end": v(0.04, 3.92) * mm});
            skLineSegment(sketch, "E107.2.92", {"start": v(-0.01, 3.92) * mm, "end": v(-0.03, 3.92) * mm});
            skLineSegment(sketch, "E107.2.93", {"start": v(-0.06, 3.92) * mm, "end": v(-0.18, 3.93) * mm});
            skLineSegment(sketch, "E107.2.94", {"start": v(-0.05, 3.92) * mm, "end": v(-0.06, 3.92) * mm});
            skLineSegment(sketch, "E107.2.95", {"start": v(-0.04, 3.92) * mm, "end": v(-0.05, 3.92) * mm});
            skLineSegment(sketch, "E107.2.96", {"start": v(-0.03, 3.92) * mm, "end": v(-0.04, 3.92) * mm});
            skLineSegment(sketch, "E107.2.97", {"start": v(0, 3.92) * mm, "end": v(-0.01, 3.92) * mm});
            skLineSegment(sketch, "E107.2.98", {"start": v(0, 3.92) * mm, "end": v(0.01, 3.92) * mm});
            skLineSegment(sketch, "E107.2.99", {"start": v(0.01, 3.92) * mm, "end": v(0.03, 3.92) * mm});
            skLineSegment(sketch, "E107.2.100", {"start": v(0.04, 3.92) * mm, "end": v(0.05, 3.92) * mm});
            skLineSegment(sketch, "E107.2.101", {"start": v(0.05, 3.92) * mm, "end": v(0.06, 3.92) * mm});
            skPoint(sketch, "E107.3.0", {"position": v(-4.03, 4.03) * mm});
            skPoint(sketch, "E107.3.1", {"position": v(-4.03, 4.03) * mm});
            skLineSegment(sketch, "E107.3.2", {"start": v(-2.82, 4.22) * mm, "end": v(-2.9, 4.3) * mm});
            skLineSegment(sketch, "E107.3.3", {"start": v(-3.23, 5.58) * mm, "end": v(-3.22, 5.68) * mm});
            skLineSegment(sketch, "E107.3.4", {"start": v(-3.23, 5.37) * mm, "end": v(-3.23, 5.47) * mm});
            skLineSegment(sketch, "E107.3.5", {"start": v(-6.1, 3.16) * mm, "end": v(-6.2, 3.13) * mm});
            skLineSegment(sketch, "E107.3.6", {"start": v(-4.54, 3.1) * mm, "end": v(-4.63, 3.14) * mm});
            skLineSegment(sketch, "E107.3.7", {"start": v(-3.2, 5.78) * mm, "end": v(-3.2, 5.89) * mm});
            skLineSegment(sketch, "E107.3.8", {"start": v(-3.96, 2.65) * mm, "end": v(-4.05, 2.7) * mm});
            skLineSegment(sketch, "E107.3.9", {"start": v(-2.56, 3.06) * mm, "end": v(-2.52, 3.15) * mm});
            skLineSegment(sketch, "E107.3.10", {"start": v(-3.18, 4.8) * mm, "end": v(-3.2, 4.9) * mm});
            skLineSegment(sketch, "E107.3.11", {"start": v(-5.37, 3.23) * mm, "end": v(-5.47, 3.23) * mm});
            skLineSegment(sketch, "E107.3.12", {"start": v(-6.32, 3.1) * mm, "end": v(-6.43, 3.08) * mm});
            skLineSegment(sketch, "E107.3.13", {"start": v(-2.49, 3.46) * mm, "end": v(-2.5, 3.54) * mm});
            skLineSegment(sketch, "E107.3.14", {"start": v(-4.71, 3.16) * mm, "end": v(-4.8, 3.18) * mm});
            skLineSegment(sketch, "E107.3.15", {"start": v(-2.7, 4.05) * mm, "end": v(-2.76, 4.13) * mm});
            skLineSegment(sketch, "E107.3.16", {"start": v(-2.6, 3.88) * mm, "end": v(-2.65, 3.96) * mm});
            skLineSegment(sketch, "E107.3.17", {"start": v(-3.1, 4.54) * mm, "end": v(-3.14, 4.63) * mm});
            skLineSegment(sketch, "E107.3.18", {"start": v(-2.51, 3.63) * mm, "end": v(-2.54, 3.71) * mm});
            skLineSegment(sketch, "E107.3.19", {"start": v(-3.1, 6.32) * mm, "end": v(-3.08, 6.43) * mm});
            skLineSegment(sketch, "E107.3.20", {"start": v(-2.5, 3.22) * mm, "end": v(-2.5, 3.3) * mm});
            skLineSegment(sketch, "E107.3.21", {"start": v(-5.58, 3.23) * mm, "end": v(-5.68, 3.22) * mm});
            skLineSegment(sketch, "E107.3.22", {"start": v(-4.9, 3.2) * mm, "end": v(-4.99, 3.21) * mm});
            skLineSegment(sketch, "E107.3.23", {"start": v(-3.16, 4.71) * mm, "end": v(-3.18, 4.8) * mm});
            skLineSegment(sketch, "E107.3.24", {"start": v(-2.65, 3.96) * mm, "end": v(-2.7, 4.05) * mm});
            skLineSegment(sketch, "E107.3.25", {"start": v(-6.2, 3.13) * mm, "end": v(-6.32, 3.1) * mm});
            skLineSegment(sketch, "E107.3.26", {"start": v(-3.2, 4.9) * mm, "end": v(-3.21, 4.99) * mm});
            skLineSegment(sketch, "E107.3.27", {"start": v(-4.63, 3.14) * mm, "end": v(-4.71, 3.16) * mm});
            skLineSegment(sketch, "E107.3.28", {"start": v(-4.05, 2.7) * mm, "end": v(-4.13, 2.76) * mm});
            skLineSegment(sketch, "E107.3.29", {"start": v(-2.9, 4.3) * mm, "end": v(-2.98, 4.38) * mm});
            skLineSegment(sketch, "E107.3.30", {"start": v(-3.22, 5.08) * mm, "end": v(-3.23, 5.18) * mm});
            skLineSegment(sketch, "E107.3.31", {"start": v(-3.22, 5.68) * mm, "end": v(-3.2, 5.78) * mm});
            skLineSegment(sketch, "E107.3.32", {"start": v(-2.57, 3.8) * mm, "end": v(-2.6, 3.88) * mm});
            skLineSegment(sketch, "E107.3.33", {"start": v(-2.52, 3.15) * mm, "end": v(-2.5, 3.22) * mm});
            skLineSegment(sketch, "E107.3.34", {"start": v(-2.5, 3.54) * mm, "end": v(-2.51, 3.63) * mm});
            skLineSegment(sketch, "E107.3.35", {"start": v(-5.47, 3.23) * mm, "end": v(-5.58, 3.23) * mm});
            skLineSegment(sketch, "E107.3.36", {"start": v(-4.8, 3.18) * mm, "end": v(-4.9, 3.2) * mm});
            skLineSegment(sketch, "E107.3.37", {"start": v(-2.5, 3.3) * mm, "end": v(-2.49, 3.38) * mm});
            skLineSegment(sketch, "E107.3.38", {"start": v(-5.68, 3.22) * mm, "end": v(-5.78, 3.2) * mm});
            skLineSegment(sketch, "E107.3.39", {"start": v(-4.99, 3.21) * mm, "end": v(-5.08, 3.22) * mm});
            skLineSegment(sketch, "E107.3.40", {"start": v(-3.21, 4.99) * mm, "end": v(-3.22, 5.08) * mm});
            skLineSegment(sketch, "E107.3.41", {"start": v(-2.8, 6.55) * mm, "end": v(-2.73, 6.58) * mm});
            skLineSegment(sketch, "E107.3.42", {"start": v(-3.46, 2.49) * mm, "end": v(-3.54, 2.5) * mm});
            skLineSegment(sketch, "E107.3.43", {"start": v(-3.54, 2.5) * mm, "end": v(-3.63, 2.51) * mm});
            skLineSegment(sketch, "E107.3.44", {"start": v(-3.63, 2.51) * mm, "end": v(-3.71, 2.54) * mm});
            skLineSegment(sketch, "E107.3.45", {"start": v(-2.9, 2.65) * mm, "end": v(-2.99, 2.6) * mm});
            skLineSegment(sketch, "E107.3.46", {"start": v(-2.99, 2.6) * mm, "end": v(-3.06, 2.56) * mm});
            skLineSegment(sketch, "E107.3.47", {"start": v(-3.06, 2.56) * mm, "end": v(-3.15, 2.52) * mm});
            skLineSegment(sketch, "E107.3.48", {"start": v(-3.15, 2.52) * mm, "end": v(-3.22, 2.5) * mm});
            skLineSegment(sketch, "E107.3.49", {"start": v(-3.22, 2.5) * mm, "end": v(-3.3, 2.5) * mm});
            skLineSegment(sketch, "E107.3.50", {"start": v(-3.3, 2.5) * mm, "end": v(-3.38, 2.49) * mm});
            skLineSegment(sketch, "E107.3.51", {"start": v(-3.38, 2.49) * mm, "end": v(-3.46, 2.49) * mm});
            skLineSegment(sketch, "E107.3.52", {"start": v(-3.23, 5.18) * mm, "end": v(-3.23, 5.27) * mm});
            skLineSegment(sketch, "E107.3.53", {"start": v(-5.78, 3.2) * mm, "end": v(-5.89, 3.2) * mm});
            skLineSegment(sketch, "E107.3.54", {"start": v(-3.2, 5.89) * mm, "end": v(-3.18, 6) * mm});
            skLineSegment(sketch, "E107.3.55", {"start": v(-2.49, 3.38) * mm, "end": v(-2.49, 3.46) * mm});
            skLineSegment(sketch, "E107.3.56", {"start": v(-3.71, 2.54) * mm, "end": v(-3.8, 2.57) * mm});
            skLineSegment(sketch, "E107.3.57", {"start": v(-3.23, 5.47) * mm, "end": v(-3.23, 5.58) * mm});
            skLineSegment(sketch, "E107.3.58", {"start": v(-5.08, 3.22) * mm, "end": v(-5.18, 3.23) * mm});
            skLineSegment(sketch, "E107.3.59", {"start": v(-5.89, 3.2) * mm, "end": v(-6, 3.18) * mm});
            skLineSegment(sketch, "E107.3.60", {"start": v(-4.38, 2.98) * mm, "end": v(-4.47, 3.07) * mm});
            skLineSegment(sketch, "E107.3.61", {"start": v(-2.98, 4.38) * mm, "end": v(-3.07, 4.47) * mm});
            skLineSegment(sketch, "E107.3.62", {"start": v(-3.14, 4.63) * mm, "end": v(-3.16, 4.71) * mm});
            skLineSegment(sketch, "E107.3.63", {"start": v(-3.8, 2.57) * mm, "end": v(-3.88, 2.6) * mm});
            skLineSegment(sketch, "E107.3.64", {"start": v(-2.54, 3.71) * mm, "end": v(-2.57, 3.8) * mm});
            skLineSegment(sketch, "E107.3.65", {"start": v(-5.18, 3.23) * mm, "end": v(-5.27, 3.23) * mm});
            skLineSegment(sketch, "E107.3.66", {"start": v(-3.18, 6) * mm, "end": v(-3.16, 6.1) * mm});
            skLineSegment(sketch, "E107.3.67", {"start": v(-6, 3.18) * mm, "end": v(-6.1, 3.16) * mm});
            skLineSegment(sketch, "E107.3.68", {"start": v(-4.47, 3.07) * mm, "end": v(-4.54, 3.1) * mm});
            skLineSegment(sketch, "E107.3.69", {"start": v(-2.76, 4.13) * mm, "end": v(-2.82, 4.22) * mm});
            skLineSegment(sketch, "E107.3.70", {"start": v(-3.13, 6.2) * mm, "end": v(-3.1, 6.32) * mm});
            skLineSegment(sketch, "E107.3.71", {"start": v(-3.88, 2.6) * mm, "end": v(-3.96, 2.65) * mm});
            skLineSegment(sketch, "E107.3.72", {"start": v(-3.16, 6.1) * mm, "end": v(-3.13, 6.2) * mm});
            skLineSegment(sketch, "E107.3.73", {"start": v(-3.23, 5.27) * mm, "end": v(-3.23, 5.37) * mm});
            skLineSegment(sketch, "E107.3.74", {"start": v(-5.27, 3.23) * mm, "end": v(-5.37, 3.23) * mm});
            skLineSegment(sketch, "E107.3.75", {"start": v(-3.07, 4.47) * mm, "end": v(-3.1, 4.54) * mm});
            skLineSegment(sketch, "E107.3.76", {"start": v(-4.13, 2.76) * mm, "end": v(-4.22, 2.82) * mm});
            skLineSegment(sketch, "E107.3.77", {"start": v(-4.22, 2.82) * mm, "end": v(-4.3, 2.9) * mm});
            skLineSegment(sketch, "E107.3.78", {"start": v(-4.3, 2.9) * mm, "end": v(-4.38, 2.98) * mm});
            skLineSegment(sketch, "E107.3.79", {"start": v(-6.55, 2.8) * mm, "end": v(-6.58, 2.73) * mm});
            skLineSegment(sketch, "E107.3.80", {"start": v(-3, 6.46) * mm, "end": v(-2.94, 6.5) * mm});
            skLineSegment(sketch, "E107.3.81", {"start": v(-2.87, 6.52) * mm, "end": v(-2.8, 6.55) * mm});
            skLineSegment(sketch, "E107.3.82", {"start": v(-2.94, 6.5) * mm, "end": v(-2.87, 6.52) * mm});
            skLineSegment(sketch, "E107.3.83", {"start": v(-6.46, 3) * mm, "end": v(-6.5, 2.94) * mm});
            skLineSegment(sketch, "E107.3.84", {"start": v(-3.08, 6.43) * mm, "end": v(-3, 6.46) * mm});
            skLineSegment(sketch, "E107.3.85", {"start": v(-6.43, 3.08) * mm, "end": v(-6.46, 3) * mm});
            skLineSegment(sketch, "E107.3.86", {"start": v(-6.5, 2.94) * mm, "end": v(-6.52, 2.87) * mm});
            skLineSegment(sketch, "E107.3.87", {"start": v(-2.65, 2.9) * mm, "end": v(-2.6, 2.99) * mm});
            skLineSegment(sketch, "E107.3.88", {"start": v(-6.52, 2.87) * mm, "end": v(-6.55, 2.8) * mm});
            skLineSegment(sketch, "E107.3.89", {"start": v(-2.6, 2.99) * mm, "end": v(-2.56, 3.06) * mm});
            skLineSegment(sketch, "E107.3.90", {"start": v(-2.73, 2.82) * mm, "end": v(-2.65, 2.9) * mm});
            skLineSegment(sketch, "E107.3.91", {"start": v(-2.75, 2.79) * mm, "end": v(-2.74, 2.8) * mm});
            skLineSegment(sketch, "E107.3.92", {"start": v(-2.78, 2.76) * mm, "end": v(-2.79, 2.75) * mm});
            skLineSegment(sketch, "E107.3.93", {"start": v(-2.82, 2.73) * mm, "end": v(-2.9, 2.65) * mm});
            skLineSegment(sketch, "E107.3.94", {"start": v(-2.8, 2.74) * mm, "end": v(-2.82, 2.73) * mm});
            skLineSegment(sketch, "E107.3.95", {"start": v(-2.8, 2.74) * mm, "end": v(-2.8, 2.74) * mm});
            skLineSegment(sketch, "E107.3.96", {"start": v(-2.79, 2.75) * mm, "end": v(-2.8, 2.74) * mm});
            skLineSegment(sketch, "E107.3.97", {"start": v(-2.77, 2.77) * mm, "end": v(-2.78, 2.76) * mm});
            skLineSegment(sketch, "E107.3.98", {"start": v(-2.77, 2.77) * mm, "end": v(-2.76, 2.78) * mm});
            skLineSegment(sketch, "E107.3.99", {"start": v(-2.76, 2.78) * mm, "end": v(-2.75, 2.79) * mm});
            skLineSegment(sketch, "E107.3.100", {"start": v(-2.74, 2.8) * mm, "end": v(-2.74, 2.8) * mm});
            skLineSegment(sketch, "E107.3.101", {"start": v(-2.74, 2.8) * mm, "end": v(-2.73, 2.82) * mm});
            skPoint(sketch, "E107.4.0", {"position": v(-5.7, 0) * mm});
            skPoint(sketch, "E107.4.1", {"position": v(-5.7, 0) * mm});
            skLineSegment(sketch, "E107.4.2", {"start": v(-4.98, 0.99) * mm, "end": v(-5.1, 1) * mm});
            skLineSegment(sketch, "E107.4.3", {"start": v(-6.23, 1.66) * mm, "end": v(-6.3, 1.74) * mm});
            skLineSegment(sketch, "E107.4.4", {"start": v(-6.09, 1.51) * mm, "end": v(-6.16, 1.58) * mm});
            skLineSegment(sketch, "E107.4.5", {"start": v(-6.55, -2.08) * mm, "end": v(-6.6, -2.17) * mm});
            skLineSegment(sketch, "E107.4.6", {"start": v(-5.41, -1.02) * mm, "end": v(-5.49, -1.06) * mm});
            skLineSegment(sketch, "E107.4.7", {"start": v(-6.36, 1.82) * mm, "end": v(-6.42, 1.9) * mm});
            skLineSegment(sketch, "E107.4.8", {"start": v(-4.67, -0.93) * mm, "end": v(-4.77, -0.96) * mm});
            skLineSegment(sketch, "E107.4.9", {"start": v(-3.97, 0.36) * mm, "end": v(-4, 0.44) * mm});
            skLineSegment(sketch, "E107.4.10", {"start": v(-5.65, 1.15) * mm, "end": v(-5.72, 1.2) * mm});
            skLineSegment(sketch, "E107.4.11", {"start": v(-6.09, -1.51) * mm, "end": v(-6.16, -1.58) * mm});
            skLineSegment(sketch, "E107.4.12", {"start": v(-6.66, -2.27) * mm, "end": v(-6.72, -2.37) * mm});
            skLineSegment(sketch, "E107.4.13", {"start": v(-4.2, 0.69) * mm, "end": v(-4.27, 0.74) * mm});
            skLineSegment(sketch, "E107.4.14", {"start": v(-5.57, -1.1) * mm, "end": v(-5.65, -1.15) * mm});
            skLineSegment(sketch, "E107.4.15", {"start": v(-4.77, 0.96) * mm, "end": v(-4.87, 0.97) * mm});
            skLineSegment(sketch, "E107.4.16", {"start": v(-4.58, 0.9) * mm, "end": v(-4.67, 0.93) * mm});
            skLineSegment(sketch, "E107.4.17", {"start": v(-5.41, 1.02) * mm, "end": v(-5.49, 1.06) * mm});
            skLineSegment(sketch, "E107.4.18", {"start": v(-4.34, 0.79) * mm, "end": v(-4.42, 0.83) * mm});
            skLineSegment(sketch, "E107.4.19", {"start": v(-6.66, 2.27) * mm, "end": v(-6.72, 2.37) * mm});
            skLineSegment(sketch, "E107.4.20", {"start": v(-4.05, 0.5) * mm, "end": v(-4.1, 0.57) * mm});
            skLineSegment(sketch, "E107.4.21", {"start": v(-6.23, -1.66) * mm, "end": v(-6.3, -1.74) * mm});
            skLineSegment(sketch, "E107.4.22", {"start": v(-5.72, -1.2) * mm, "end": v(-5.8, -1.25) * mm});
            skLineSegment(sketch, "E107.4.23", {"start": v(-5.57, 1.1) * mm, "end": v(-5.65, 1.15) * mm});
            skLineSegment(sketch, "E107.4.24", {"start": v(-4.67, 0.93) * mm, "end": v(-4.77, 0.96) * mm});
            skLineSegment(sketch, "E107.4.25", {"start": v(-6.6, -2.17) * mm, "end": v(-6.66, -2.27) * mm});
            skLineSegment(sketch, "E107.4.26", {"start": v(-5.72, 1.2) * mm, "end": v(-5.8, 1.25) * mm});
            skLineSegment(sketch, "E107.4.27", {"start": v(-5.49, -1.06) * mm, "end": v(-5.57, -1.1) * mm});
            skLineSegment(sketch, "E107.4.28", {"start": v(-4.77, -0.96) * mm, "end": v(-4.87, -0.97) * mm});
            skLineSegment(sketch, "E107.4.29", {"start": v(-5.1, 1) * mm, "end": v(-5.2, 0.99) * mm});
            skLineSegment(sketch, "E107.4.30", {"start": v(-5.87, 1.31) * mm, "end": v(-5.94, 1.38) * mm});
            skLineSegment(sketch, "E107.4.31", {"start": v(-6.3, 1.74) * mm, "end": v(-6.36, 1.82) * mm});
            skLineSegment(sketch, "E107.4.32", {"start": v(-4.5, 0.87) * mm, "end": v(-4.58, 0.9) * mm});
            skLineSegment(sketch, "E107.4.33", {"start": v(-4, 0.44) * mm, "end": v(-4.05, 0.5) * mm});
            skLineSegment(sketch, "E107.4.34", {"start": v(-4.27, 0.74) * mm, "end": v(-4.34, 0.79) * mm});
            skLineSegment(sketch, "E107.4.35", {"start": v(-6.16, -1.58) * mm, "end": v(-6.23, -1.66) * mm});
            skLineSegment(sketch, "E107.4.36", {"start": v(-5.65, -1.15) * mm, "end": v(-5.72, -1.2) * mm});
            skLineSegment(sketch, "E107.4.37", {"start": v(-4.1, 0.57) * mm, "end": v(-4.15, 0.63) * mm});
            skLineSegment(sketch, "E107.4.38", {"start": v(-6.3, -1.74) * mm, "end": v(-6.36, -1.82) * mm});
            skLineSegment(sketch, "E107.4.39", {"start": v(-5.8, -1.25) * mm, "end": v(-5.87, -1.31) * mm});
            skLineSegment(sketch, "E107.4.40", {"start": v(-5.8, 1.25) * mm, "end": v(-5.87, 1.31) * mm});
            skLineSegment(sketch, "E107.4.41", {"start": v(-6.61, 2.66) * mm, "end": v(-6.58, 2.73) * mm});
            skLineSegment(sketch, "E107.4.42", {"start": v(-4.2, -0.69) * mm, "end": v(-4.27, -0.74) * mm});
            skLineSegment(sketch, "E107.4.43", {"start": v(-4.27, -0.74) * mm, "end": v(-4.34, -0.79) * mm});
            skLineSegment(sketch, "E107.4.44", {"start": v(-4.34, -0.79) * mm, "end": v(-4.42, -0.83) * mm});
            skLineSegment(sketch, "E107.4.45", {"start": v(-3.93, -0.18) * mm, "end": v(-3.95, -0.28) * mm});
            skLineSegment(sketch, "E107.4.46", {"start": v(-3.95, -0.28) * mm, "end": v(-3.97, -0.36) * mm});
            skLineSegment(sketch, "E107.4.47", {"start": v(-3.97, -0.36) * mm, "end": v(-4, -0.44) * mm});
            skLineSegment(sketch, "E107.4.48", {"start": v(-4, -0.44) * mm, "end": v(-4.05, -0.5) * mm});
            skLineSegment(sketch, "E107.4.49", {"start": v(-4.05, -0.5) * mm, "end": v(-4.1, -0.57) * mm});
            skLineSegment(sketch, "E107.4.50", {"start": v(-4.1, -0.57) * mm, "end": v(-4.15, -0.63) * mm});
            skLineSegment(sketch, "E107.4.51", {"start": v(-4.15, -0.63) * mm, "end": v(-4.2, -0.69) * mm});
            skLineSegment(sketch, "E107.4.52", {"start": v(-5.94, 1.38) * mm, "end": v(-6.02, 1.44) * mm});
            skLineSegment(sketch, "E107.4.53", {"start": v(-6.36, -1.82) * mm, "end": v(-6.42, -1.9) * mm});
            skLineSegment(sketch, "E107.4.54", {"start": v(-6.42, 1.9) * mm, "end": v(-6.48, 2) * mm});
            skLineSegment(sketch, "E107.4.55", {"start": v(-4.15, 0.63) * mm, "end": v(-4.2, 0.69) * mm});
            skLineSegment(sketch, "E107.4.56", {"start": v(-4.42, -0.83) * mm, "end": v(-4.5, -0.87) * mm});
            skLineSegment(sketch, "E107.4.57", {"start": v(-6.16, 1.58) * mm, "end": v(-6.23, 1.66) * mm});
            skLineSegment(sketch, "E107.4.58", {"start": v(-5.87, -1.31) * mm, "end": v(-5.94, -1.38) * mm});
            skLineSegment(sketch, "E107.4.59", {"start": v(-6.42, -1.9) * mm, "end": v(-6.48, -2) * mm});
            skLineSegment(sketch, "E107.4.60", {"start": v(-5.2, -0.99) * mm, "end": v(-5.33, -0.99) * mm});
            skLineSegment(sketch, "E107.4.61", {"start": v(-5.2, 0.99) * mm, "end": v(-5.33, 0.99) * mm});
            skLineSegment(sketch, "E107.4.62", {"start": v(-5.49, 1.06) * mm, "end": v(-5.57, 1.1) * mm});
            skLineSegment(sketch, "E107.4.63", {"start": v(-4.5, -0.87) * mm, "end": v(-4.58, -0.9) * mm});
            skLineSegment(sketch, "E107.4.64", {"start": v(-4.42, 0.83) * mm, "end": v(-4.5, 0.87) * mm});
            skLineSegment(sketch, "E107.4.65", {"start": v(-5.94, -1.38) * mm, "end": v(-6.02, -1.44) * mm});
            skLineSegment(sketch, "E107.4.66", {"start": v(-6.48, 2) * mm, "end": v(-6.55, 2.08) * mm});
            skLineSegment(sketch, "E107.4.67", {"start": v(-6.48, -2) * mm, "end": v(-6.55, -2.08) * mm});
            skLineSegment(sketch, "E107.4.68", {"start": v(-5.33, -0.99) * mm, "end": v(-5.41, -1.02) * mm});
            skLineSegment(sketch, "E107.4.69", {"start": v(-4.87, 0.97) * mm, "end": v(-4.98, 0.99) * mm});
            skLineSegment(sketch, "E107.4.70", {"start": v(-6.6, 2.17) * mm, "end": v(-6.66, 2.27) * mm});
            skLineSegment(sketch, "E107.4.71", {"start": v(-4.58, -0.9) * mm, "end": v(-4.67, -0.93) * mm});
            skLineSegment(sketch, "E107.4.72", {"start": v(-6.55, 2.08) * mm, "end": v(-6.6, 2.17) * mm});
            skLineSegment(sketch, "E107.4.73", {"start": v(-6.02, 1.44) * mm, "end": v(-6.09, 1.51) * mm});
            skLineSegment(sketch, "E107.4.74", {"start": v(-6.02, -1.44) * mm, "end": v(-6.09, -1.51) * mm});
            skLineSegment(sketch, "E107.4.75", {"start": v(-5.33, 0.99) * mm, "end": v(-5.41, 1.02) * mm});
            skLineSegment(sketch, "E107.4.76", {"start": v(-4.87, -0.97) * mm, "end": v(-4.98, -0.99) * mm});
            skLineSegment(sketch, "E107.4.77", {"start": v(-4.98, -0.99) * mm, "end": v(-5.1, -1) * mm});
            skLineSegment(sketch, "E107.4.78", {"start": v(-5.1, -1) * mm, "end": v(-5.2, -0.99) * mm});
            skLineSegment(sketch, "E107.4.79", {"start": v(-6.61, -2.66) * mm, "end": v(-6.58, -2.73) * mm});
            skLineSegment(sketch, "E107.4.80", {"start": v(-6.7, 2.44) * mm, "end": v(-6.67, 2.51) * mm});
            skLineSegment(sketch, "E107.4.81", {"start": v(-6.64, 2.58) * mm, "end": v(-6.61, 2.66) * mm});
            skLineSegment(sketch, "E107.4.82", {"start": v(-6.67, 2.51) * mm, "end": v(-6.64, 2.58) * mm});
            skLineSegment(sketch, "E107.4.83", {"start": v(-6.7, -2.44) * mm, "end": v(-6.67, -2.51) * mm});
            skLineSegment(sketch, "E107.4.84", {"start": v(-6.72, 2.37) * mm, "end": v(-6.7, 2.44) * mm});
            skLineSegment(sketch, "E107.4.85", {"start": v(-6.72, -2.37) * mm, "end": v(-6.7, -2.44) * mm});
            skLineSegment(sketch, "E107.4.86", {"start": v(-6.67, -2.51) * mm, "end": v(-6.64, -2.58) * mm});
            skLineSegment(sketch, "E107.4.87", {"start": v(-3.93, 0.18) * mm, "end": v(-3.95, 0.28) * mm});
            skLineSegment(sketch, "E107.4.88", {"start": v(-6.64, -2.58) * mm, "end": v(-6.61, -2.66) * mm});
            skLineSegment(sketch, "E107.4.89", {"start": v(-3.95, 0.28) * mm, "end": v(-3.97, 0.36) * mm});
            skLineSegment(sketch, "E107.4.90", {"start": v(-3.92, 0.06) * mm, "end": v(-3.93, 0.18) * mm});
            skLineSegment(sketch, "E107.4.91", {"start": v(-3.92, 0.03) * mm, "end": v(-3.92, 0.04) * mm});
            skLineSegment(sketch, "E107.4.92", {"start": v(-3.92, -0.01) * mm, "end": v(-3.92, -0.03) * mm});
            skLineSegment(sketch, "E107.4.93", {"start": v(-3.92, -0.06) * mm, "end": v(-3.93, -0.18) * mm});
            skLineSegment(sketch, "E107.4.94", {"start": v(-3.92, -0.05) * mm, "end": v(-3.92, -0.06) * mm});
            skLineSegment(sketch, "E107.4.95", {"start": v(-3.92, -0.04) * mm, "end": v(-3.92, -0.05) * mm});
            skLineSegment(sketch, "E107.4.96", {"start": v(-3.92, -0.03) * mm, "end": v(-3.92, -0.04) * mm});
            skLineSegment(sketch, "E107.4.97", {"start": v(-3.92, 0) * mm, "end": v(-3.92, -0.01) * mm});
            skLineSegment(sketch, "E107.4.98", {"start": v(-3.92, 0) * mm, "end": v(-3.92, 0.01) * mm});
            skLineSegment(sketch, "E107.4.99", {"start": v(-3.92, 0.01) * mm, "end": v(-3.92, 0.03) * mm});
            skLineSegment(sketch, "E107.4.100", {"start": v(-3.92, 0.04) * mm, "end": v(-3.92, 0.05) * mm});
            skLineSegment(sketch, "E107.4.101", {"start": v(-3.92, 0.05) * mm, "end": v(-3.92, 0.06) * mm});
            skPoint(sketch, "E107.5.0", {"position": v(-4.03, -4.03) * mm});
            skPoint(sketch, "E107.5.1", {"position": v(-4.03, -4.03) * mm});
            skLineSegment(sketch, "E107.5.2", {"start": v(-4.22, -2.82) * mm, "end": v(-4.3, -2.9) * mm});
            skLineSegment(sketch, "E107.5.3", {"start": v(-5.58, -3.23) * mm, "end": v(-5.68, -3.22) * mm});
            skLineSegment(sketch, "E107.5.4", {"start": v(-5.37, -3.23) * mm, "end": v(-5.47, -3.23) * mm});
            skLineSegment(sketch, "E107.5.5", {"start": v(-3.16, -6.1) * mm, "end": v(-3.13, -6.2) * mm});
            skLineSegment(sketch, "E107.5.6", {"start": v(-3.1, -4.54) * mm, "end": v(-3.14, -4.63) * mm});
            skLineSegment(sketch, "E107.5.7", {"start": v(-5.78, -3.2) * mm, "end": v(-5.89, -3.2) * mm});
            skLineSegment(sketch, "E107.5.8", {"start": v(-2.65, -3.96) * mm, "end": v(-2.7, -4.05) * mm});
            skLineSegment(sketch, "E107.5.9", {"start": v(-3.06, -2.56) * mm, "end": v(-3.15, -2.52) * mm});
            skLineSegment(sketch, "E107.5.10", {"start": v(-4.8, -3.18) * mm, "end": v(-4.9, -3.2) * mm});
            skLineSegment(sketch, "E107.5.11", {"start": v(-3.23, -5.37) * mm, "end": v(-3.23, -5.47) * mm});
            skLineSegment(sketch, "E107.5.12", {"start": v(-3.1, -6.32) * mm, "end": v(-3.08, -6.43) * mm});
            skLineSegment(sketch, "E107.5.13", {"start": v(-3.46, -2.49) * mm, "end": v(-3.54, -2.5) * mm});
            skLineSegment(sketch, "E107.5.14", {"start": v(-3.16, -4.71) * mm, "end": v(-3.18, -4.8) * mm});
            skLineSegment(sketch, "E107.5.15", {"start": v(-4.05, -2.7) * mm, "end": v(-4.13, -2.76) * mm});
            skLineSegment(sketch, "E107.5.16", {"start": v(-3.88, -2.6) * mm, "end": v(-3.96, -2.65) * mm});
            skLineSegment(sketch, "E107.5.17", {"start": v(-4.54, -3.1) * mm, "end": v(-4.63, -3.14) * mm});
            skLineSegment(sketch, "E107.5.18", {"start": v(-3.63, -2.51) * mm, "end": v(-3.71, -2.54) * mm});
            skLineSegment(sketch, "E107.5.19", {"start": v(-6.32, -3.1) * mm, "end": v(-6.43, -3.08) * mm});
            skLineSegment(sketch, "E107.5.20", {"start": v(-3.22, -2.5) * mm, "end": v(-3.3, -2.5) * mm});
            skLineSegment(sketch, "E107.5.21", {"start": v(-3.23, -5.58) * mm, "end": v(-3.22, -5.68) * mm});
            skLineSegment(sketch, "E107.5.22", {"start": v(-3.2, -4.9) * mm, "end": v(-3.21, -4.99) * mm});
            skLineSegment(sketch, "E107.5.23", {"start": v(-4.71, -3.16) * mm, "end": v(-4.8, -3.18) * mm});
            skLineSegment(sketch, "E107.5.24", {"start": v(-3.96, -2.65) * mm, "end": v(-4.05, -2.7) * mm});
            skLineSegment(sketch, "E107.5.25", {"start": v(-3.13, -6.2) * mm, "end": v(-3.1, -6.32) * mm});
            skLineSegment(sketch, "E107.5.26", {"start": v(-4.9, -3.2) * mm, "end": v(-4.99, -3.21) * mm});
            skLineSegment(sketch, "E107.5.27", {"start": v(-3.14, -4.63) * mm, "end": v(-3.16, -4.71) * mm});
            skLineSegment(sketch, "E107.5.28", {"start": v(-2.7, -4.05) * mm, "end": v(-2.76, -4.13) * mm});
            skLineSegment(sketch, "E107.5.29", {"start": v(-4.3, -2.9) * mm, "end": v(-4.38, -2.98) * mm});
            skLineSegment(sketch, "E107.5.30", {"start": v(-5.08, -3.22) * mm, "end": v(-5.18, -3.23) * mm});
            skLineSegment(sketch, "E107.5.31", {"start": v(-5.68, -3.22) * mm, "end": v(-5.78, -3.2) * mm});
            skLineSegment(sketch, "E107.5.32", {"start": v(-3.8, -2.57) * mm, "end": v(-3.88, -2.6) * mm});
            skLineSegment(sketch, "E107.5.33", {"start": v(-3.15, -2.52) * mm, "end": v(-3.22, -2.5) * mm});
            skLineSegment(sketch, "E107.5.34", {"start": v(-3.54, -2.5) * mm, "end": v(-3.63, -2.51) * mm});
            skLineSegment(sketch, "E107.5.35", {"start": v(-3.23, -5.47) * mm, "end": v(-3.23, -5.58) * mm});
            skLineSegment(sketch, "E107.5.36", {"start": v(-3.18, -4.8) * mm, "end": v(-3.2, -4.9) * mm});
            skLineSegment(sketch, "E107.5.37", {"start": v(-3.3, -2.5) * mm, "end": v(-3.38, -2.49) * mm});
            skLineSegment(sketch, "E107.5.38", {"start": v(-3.22, -5.68) * mm, "end": v(-3.2, -5.78) * mm});
            skLineSegment(sketch, "E107.5.39", {"start": v(-3.21, -4.99) * mm, "end": v(-3.22, -5.08) * mm});
            skLineSegment(sketch, "E107.5.40", {"start": v(-4.99, -3.21) * mm, "end": v(-5.08, -3.22) * mm});
            skLineSegment(sketch, "E107.5.41", {"start": v(-6.55, -2.8) * mm, "end": v(-6.58, -2.73) * mm});
            skLineSegment(sketch, "E107.5.42", {"start": v(-2.49, -3.46) * mm, "end": v(-2.5, -3.54) * mm});
            skLineSegment(sketch, "E107.5.43", {"start": v(-2.5, -3.54) * mm, "end": v(-2.51, -3.63) * mm});
            skLineSegment(sketch, "E107.5.44", {"start": v(-2.51, -3.63) * mm, "end": v(-2.54, -3.71) * mm});
            skLineSegment(sketch, "E107.5.45", {"start": v(-2.65, -2.9) * mm, "end": v(-2.6, -2.99) * mm});
            skLineSegment(sketch, "E107.5.46", {"start": v(-2.6, -2.99) * mm, "end": v(-2.56, -3.06) * mm});
            skLineSegment(sketch, "E107.5.47", {"start": v(-2.56, -3.06) * mm, "end": v(-2.52, -3.15) * mm});
            skLineSegment(sketch, "E107.5.48", {"start": v(-2.52, -3.15) * mm, "end": v(-2.5, -3.22) * mm});
            skLineSegment(sketch, "E107.5.49", {"start": v(-2.5, -3.22) * mm, "end": v(-2.5, -3.3) * mm});
            skLineSegment(sketch, "E107.5.50", {"start": v(-2.5, -3.3) * mm, "end": v(-2.49, -3.38) * mm});
            skLineSegment(sketch, "E107.5.51", {"start": v(-2.49, -3.38) * mm, "end": v(-2.49, -3.46) * mm});
            skLineSegment(sketch, "E107.5.52", {"start": v(-5.18, -3.23) * mm, "end": v(-5.27, -3.23) * mm});
            skLineSegment(sketch, "E107.5.53", {"start": v(-3.2, -5.78) * mm, "end": v(-3.2, -5.89) * mm});
            skLineSegment(sketch, "E107.5.54", {"start": v(-5.89, -3.2) * mm, "end": v(-6, -3.18) * mm});
            skLineSegment(sketch, "E107.5.55", {"start": v(-3.38, -2.49) * mm, "end": v(-3.46, -2.49) * mm});
            skLineSegment(sketch, "E107.5.56", {"start": v(-2.54, -3.71) * mm, "end": v(-2.57, -3.8) * mm});
            skLineSegment(sketch, "E107.5.57", {"start": v(-5.47, -3.23) * mm, "end": v(-5.58, -3.23) * mm});
            skLineSegment(sketch, "E107.5.58", {"start": v(-3.22, -5.08) * mm, "end": v(-3.23, -5.18) * mm});
            skLineSegment(sketch, "E107.5.59", {"start": v(-3.2, -5.89) * mm, "end": v(-3.18, -6) * mm});
            skLineSegment(sketch, "E107.5.60", {"start": v(-2.98, -4.38) * mm, "end": v(-3.07, -4.47) * mm});
            skLineSegment(sketch, "E107.5.61", {"start": v(-4.38, -2.98) * mm, "end": v(-4.47, -3.07) * mm});
            skLineSegment(sketch, "E107.5.62", {"start": v(-4.63, -3.14) * mm, "end": v(-4.71, -3.16) * mm});
            skLineSegment(sketch, "E107.5.63", {"start": v(-2.57, -3.8) * mm, "end": v(-2.6, -3.88) * mm});
            skLineSegment(sketch, "E107.5.64", {"start": v(-3.71, -2.54) * mm, "end": v(-3.8, -2.57) * mm});
            skLineSegment(sketch, "E107.5.65", {"start": v(-3.23, -5.18) * mm, "end": v(-3.23, -5.27) * mm});
            skLineSegment(sketch, "E107.5.66", {"start": v(-6, -3.18) * mm, "end": v(-6.1, -3.16) * mm});
            skLineSegment(sketch, "E107.5.67", {"start": v(-3.18, -6) * mm, "end": v(-3.16, -6.1) * mm});
            skLineSegment(sketch, "E107.5.68", {"start": v(-3.07, -4.47) * mm, "end": v(-3.1, -4.54) * mm});
            skLineSegment(sketch, "E107.5.69", {"start": v(-4.13, -2.76) * mm, "end": v(-4.22, -2.82) * mm});
            skLineSegment(sketch, "E107.5.70", {"start": v(-6.2, -3.13) * mm, "end": v(-6.32, -3.1) * mm});
            skLineSegment(sketch, "E107.5.71", {"start": v(-2.6, -3.88) * mm, "end": v(-2.65, -3.96) * mm});
            skLineSegment(sketch, "E107.5.72", {"start": v(-6.1, -3.16) * mm, "end": v(-6.2, -3.13) * mm});
            skLineSegment(sketch, "E107.5.73", {"start": v(-5.27, -3.23) * mm, "end": v(-5.37, -3.23) * mm});
            skLineSegment(sketch, "E107.5.74", {"start": v(-3.23, -5.27) * mm, "end": v(-3.23, -5.37) * mm});
            skLineSegment(sketch, "E107.5.75", {"start": v(-4.47, -3.07) * mm, "end": v(-4.54, -3.1) * mm});
            skLineSegment(sketch, "E107.5.76", {"start": v(-2.76, -4.13) * mm, "end": v(-2.82, -4.22) * mm});
            skLineSegment(sketch, "E107.5.77", {"start": v(-2.82, -4.22) * mm, "end": v(-2.9, -4.3) * mm});
            skLineSegment(sketch, "E107.5.78", {"start": v(-2.9, -4.3) * mm, "end": v(-2.98, -4.38) * mm});
            skLineSegment(sketch, "E107.5.79", {"start": v(-2.8, -6.55) * mm, "end": v(-2.73, -6.58) * mm});
            skLineSegment(sketch, "E107.5.80", {"start": v(-6.46, -3) * mm, "end": v(-6.5, -2.94) * mm});
            skLineSegment(sketch, "E107.5.81", {"start": v(-6.52, -2.87) * mm, "end": v(-6.55, -2.8) * mm});
            skLineSegment(sketch, "E107.5.82", {"start": v(-6.5, -2.94) * mm, "end": v(-6.52, -2.87) * mm});
            skLineSegment(sketch, "E107.5.83", {"start": v(-3, -6.46) * mm, "end": v(-2.94, -6.5) * mm});
            skLineSegment(sketch, "E107.5.84", {"start": v(-6.43, -3.08) * mm, "end": v(-6.46, -3) * mm});
            skLineSegment(sketch, "E107.5.85", {"start": v(-3.08, -6.43) * mm, "end": v(-3, -6.46) * mm});
            skLineSegment(sketch, "E107.5.86", {"start": v(-2.94, -6.5) * mm, "end": v(-2.87, -6.52) * mm});
            skLineSegment(sketch, "E107.5.87", {"start": v(-2.9, -2.65) * mm, "end": v(-2.99, -2.6) * mm});
            skLineSegment(sketch, "E107.5.88", {"start": v(-2.87, -6.52) * mm, "end": v(-2.8, -6.55) * mm});
            skLineSegment(sketch, "E107.5.89", {"start": v(-2.99, -2.6) * mm, "end": v(-3.06, -2.56) * mm});
            skLineSegment(sketch, "E107.5.90", {"start": v(-2.82, -2.73) * mm, "end": v(-2.9, -2.65) * mm});
            skLineSegment(sketch, "E107.5.91", {"start": v(-2.79, -2.75) * mm, "end": v(-2.8, -2.74) * mm});
            skLineSegment(sketch, "E107.5.92", {"start": v(-2.76, -2.78) * mm, "end": v(-2.75, -2.79) * mm});
            skLineSegment(sketch, "E107.5.93", {"start": v(-2.73, -2.82) * mm, "end": v(-2.65, -2.9) * mm});
            skLineSegment(sketch, "E107.5.94", {"start": v(-2.74, -2.8) * mm, "end": v(-2.73, -2.82) * mm});
            skLineSegment(sketch, "E107.5.95", {"start": v(-2.74, -2.8) * mm, "end": v(-2.74, -2.8) * mm});
            skLineSegment(sketch, "E107.5.96", {"start": v(-2.75, -2.79) * mm, "end": v(-2.74, -2.8) * mm});
            skLineSegment(sketch, "E107.5.97", {"start": v(-2.77, -2.77) * mm, "end": v(-2.76, -2.78) * mm});
            skLineSegment(sketch, "E107.5.98", {"start": v(-2.77, -2.77) * mm, "end": v(-2.78, -2.76) * mm});
            skLineSegment(sketch, "E107.5.99", {"start": v(-2.78, -2.76) * mm, "end": v(-2.79, -2.75) * mm});
            skLineSegment(sketch, "E107.5.100", {"start": v(-2.8, -2.74) * mm, "end": v(-2.8, -2.74) * mm});
            skLineSegment(sketch, "E107.5.101", {"start": v(-2.8, -2.74) * mm, "end": v(-2.82, -2.73) * mm});
            skLineSegment(sketch, "E107.6.2", {"start": v(-0.99, -4.98) * mm, "end": v(-1, -5.1) * mm});
            skLineSegment(sketch, "E107.6.3", {"start": v(-1.66, -6.23) * mm, "end": v(-1.74, -6.3) * mm});
            skLineSegment(sketch, "E107.6.4", {"start": v(-1.51, -6.09) * mm, "end": v(-1.58, -6.16) * mm});
            skLineSegment(sketch, "E107.6.5", {"start": v(2.08, -6.55) * mm, "end": v(2.17, -6.6) * mm});
            skLineSegment(sketch, "E107.6.6", {"start": v(1.02, -5.41) * mm, "end": v(1.06, -5.49) * mm});
            skLineSegment(sketch, "E107.6.7", {"start": v(-1.82, -6.36) * mm, "end": v(-1.9, -6.42) * mm});
            skLineSegment(sketch, "E107.6.8", {"start": v(0.93, -4.67) * mm, "end": v(0.96, -4.77) * mm});
            skLineSegment(sketch, "E107.6.9", {"start": v(-0.36, -3.97) * mm, "end": v(-0.44, -4) * mm});
            skLineSegment(sketch, "E107.6.10", {"start": v(-1.15, -5.65) * mm, "end": v(-1.2, -5.72) * mm});
            skLineSegment(sketch, "E107.6.11", {"start": v(1.51, -6.09) * mm, "end": v(1.58, -6.16) * mm});
            skLineSegment(sketch, "E107.6.12", {"start": v(2.27, -6.66) * mm, "end": v(2.37, -6.72) * mm});
            skLineSegment(sketch, "E107.6.13", {"start": v(-0.69, -4.2) * mm, "end": v(-0.74, -4.27) * mm});
            skLineSegment(sketch, "E107.6.14", {"start": v(1.1, -5.57) * mm, "end": v(1.15, -5.65) * mm});
            skLineSegment(sketch, "E107.6.15", {"start": v(-0.96, -4.77) * mm, "end": v(-0.97, -4.87) * mm});
            skLineSegment(sketch, "E107.6.16", {"start": v(-0.9, -4.58) * mm, "end": v(-0.93, -4.67) * mm});
            skLineSegment(sketch, "E107.6.17", {"start": v(-1.02, -5.41) * mm, "end": v(-1.06, -5.49) * mm});
            skLineSegment(sketch, "E107.6.18", {"start": v(-0.79, -4.34) * mm, "end": v(-0.83, -4.42) * mm});
            skLineSegment(sketch, "E107.6.19", {"start": v(-2.27, -6.66) * mm, "end": v(-2.37, -6.72) * mm});
            skLineSegment(sketch, "E107.6.20", {"start": v(-0.5, -4.05) * mm, "end": v(-0.57, -4.1) * mm});
            skLineSegment(sketch, "E107.6.21", {"start": v(1.66, -6.23) * mm, "end": v(1.74, -6.3) * mm});
            skLineSegment(sketch, "E107.6.22", {"start": v(1.2, -5.72) * mm, "end": v(1.25, -5.8) * mm});
            skLineSegment(sketch, "E107.6.23", {"start": v(-1.1, -5.57) * mm, "end": v(-1.15, -5.65) * mm});
            skLineSegment(sketch, "E107.6.24", {"start": v(-0.93, -4.67) * mm, "end": v(-0.96, -4.77) * mm});
            skLineSegment(sketch, "E107.6.25", {"start": v(2.17, -6.6) * mm, "end": v(2.27, -6.66) * mm});
            skLineSegment(sketch, "E107.6.26", {"start": v(-1.2, -5.72) * mm, "end": v(-1.25, -5.8) * mm});
            skLineSegment(sketch, "E107.6.27", {"start": v(1.06, -5.49) * mm, "end": v(1.1, -5.57) * mm});
            skLineSegment(sketch, "E107.6.28", {"start": v(0.96, -4.77) * mm, "end": v(0.97, -4.87) * mm});
            skLineSegment(sketch, "E107.6.29", {"start": v(-1, -5.1) * mm, "end": v(-0.99, -5.2) * mm});
            skLineSegment(sketch, "E107.6.30", {"start": v(-1.31, -5.87) * mm, "end": v(-1.38, -5.94) * mm});
            skLineSegment(sketch, "E107.6.31", {"start": v(-1.74, -6.3) * mm, "end": v(-1.82, -6.36) * mm});
            skLineSegment(sketch, "E107.6.32", {"start": v(-0.87, -4.5) * mm, "end": v(-0.9, -4.58) * mm});
            skLineSegment(sketch, "E107.6.33", {"start": v(-0.44, -4) * mm, "end": v(-0.5, -4.05) * mm});
            skLineSegment(sketch, "E107.6.34", {"start": v(-0.74, -4.27) * mm, "end": v(-0.79, -4.34) * mm});
            skLineSegment(sketch, "E107.6.35", {"start": v(1.58, -6.16) * mm, "end": v(1.66, -6.23) * mm});
            skLineSegment(sketch, "E107.6.36", {"start": v(1.15, -5.65) * mm, "end": v(1.2, -5.72) * mm});
            skLineSegment(sketch, "E107.6.37", {"start": v(-0.57, -4.1) * mm, "end": v(-0.63, -4.15) * mm});
            skLineSegment(sketch, "E107.6.38", {"start": v(1.74, -6.3) * mm, "end": v(1.82, -6.36) * mm});
            skLineSegment(sketch, "E107.6.39", {"start": v(1.25, -5.8) * mm, "end": v(1.31, -5.87) * mm});
            skLineSegment(sketch, "E107.6.40", {"start": v(-1.25, -5.8) * mm, "end": v(-1.31, -5.87) * mm});
            skLineSegment(sketch, "E107.6.41", {"start": v(-2.66, -6.61) * mm, "end": v(-2.73, -6.58) * mm});
            skLineSegment(sketch, "E107.6.42", {"start": v(0.69, -4.2) * mm, "end": v(0.74, -4.27) * mm});
            skLineSegment(sketch, "E107.6.43", {"start": v(0.74, -4.27) * mm, "end": v(0.79, -4.34) * mm});
            skLineSegment(sketch, "E107.6.44", {"start": v(0.79, -4.34) * mm, "end": v(0.83, -4.42) * mm});
            skLineSegment(sketch, "E107.6.45", {"start": v(0.18, -3.93) * mm, "end": v(0.28, -3.95) * mm});
            skLineSegment(sketch, "E107.6.46", {"start": v(0.28, -3.95) * mm, "end": v(0.36, -3.97) * mm});
            skLineSegment(sketch, "E107.6.47", {"start": v(0.36, -3.97) * mm, "end": v(0.44, -4) * mm});
            skLineSegment(sketch, "E107.6.48", {"start": v(0.44, -4) * mm, "end": v(0.5, -4.05) * mm});
            skLineSegment(sketch, "E107.6.49", {"start": v(0.5, -4.05) * mm, "end": v(0.57, -4.1) * mm});
            skLineSegment(sketch, "E107.6.50", {"start": v(0.57, -4.1) * mm, "end": v(0.63, -4.15) * mm});
            skLineSegment(sketch, "E107.6.51", {"start": v(0.63, -4.15) * mm, "end": v(0.69, -4.2) * mm});
            skLineSegment(sketch, "E107.6.52", {"start": v(-1.38, -5.94) * mm, "end": v(-1.44, -6.02) * mm});
            skLineSegment(sketch, "E107.6.53", {"start": v(1.82, -6.36) * mm, "end": v(1.9, -6.42) * mm});
            skLineSegment(sketch, "E107.6.54", {"start": v(-1.9, -6.42) * mm, "end": v(-2, -6.48) * mm});
            skLineSegment(sketch, "E107.6.55", {"start": v(-0.63, -4.15) * mm, "end": v(-0.69, -4.2) * mm});
            skLineSegment(sketch, "E107.6.56", {"start": v(0.83, -4.42) * mm, "end": v(0.87, -4.5) * mm});
            skLineSegment(sketch, "E107.6.57", {"start": v(-1.58, -6.16) * mm, "end": v(-1.66, -6.23) * mm});
            skLineSegment(sketch, "E107.6.58", {"start": v(1.31, -5.87) * mm, "end": v(1.38, -5.94) * mm});
            skLineSegment(sketch, "E107.6.59", {"start": v(1.9, -6.42) * mm, "end": v(2, -6.48) * mm});
            skLineSegment(sketch, "E107.6.60", {"start": v(0.99, -5.2) * mm, "end": v(0.99, -5.33) * mm});
            skLineSegment(sketch, "E107.6.61", {"start": v(-0.99, -5.2) * mm, "end": v(-0.99, -5.33) * mm});
            skLineSegment(sketch, "E107.6.62", {"start": v(-1.06, -5.49) * mm, "end": v(-1.1, -5.57) * mm});
            skLineSegment(sketch, "E107.6.63", {"start": v(0.87, -4.5) * mm, "end": v(0.9, -4.58) * mm});
            skLineSegment(sketch, "E107.6.64", {"start": v(-0.83, -4.42) * mm, "end": v(-0.87, -4.5) * mm});
            skLineSegment(sketch, "E107.6.65", {"start": v(1.38, -5.94) * mm, "end": v(1.44, -6.02) * mm});
            skLineSegment(sketch, "E107.6.66", {"start": v(-2, -6.48) * mm, "end": v(-2.08, -6.55) * mm});
            skLineSegment(sketch, "E107.6.67", {"start": v(2, -6.48) * mm, "end": v(2.08, -6.55) * mm});
            skLineSegment(sketch, "E107.6.68", {"start": v(0.99, -5.33) * mm, "end": v(1.02, -5.41) * mm});
            skLineSegment(sketch, "E107.6.69", {"start": v(-0.97, -4.87) * mm, "end": v(-0.99, -4.98) * mm});
            skLineSegment(sketch, "E107.6.70", {"start": v(-2.17, -6.6) * mm, "end": v(-2.27, -6.66) * mm});
            skLineSegment(sketch, "E107.6.71", {"start": v(0.9, -4.58) * mm, "end": v(0.93, -4.67) * mm});
            skLineSegment(sketch, "E107.6.72", {"start": v(-2.08, -6.55) * mm, "end": v(-2.17, -6.6) * mm});
            skLineSegment(sketch, "E107.6.73", {"start": v(-1.44, -6.02) * mm, "end": v(-1.51, -6.09) * mm});
            skLineSegment(sketch, "E107.6.74", {"start": v(1.44, -6.02) * mm, "end": v(1.51, -6.09) * mm});
            skLineSegment(sketch, "E107.6.75", {"start": v(-0.99, -5.33) * mm, "end": v(-1.02, -5.41) * mm});
            skLineSegment(sketch, "E107.6.76", {"start": v(0.97, -4.87) * mm, "end": v(0.99, -4.98) * mm});
            skLineSegment(sketch, "E107.6.77", {"start": v(0.99, -4.98) * mm, "end": v(1, -5.1) * mm});
            skLineSegment(sketch, "E107.6.78", {"start": v(1, -5.1) * mm, "end": v(0.99, -5.2) * mm});
            skLineSegment(sketch, "E107.6.79", {"start": v(2.66, -6.61) * mm, "end": v(2.73, -6.58) * mm});
            skLineSegment(sketch, "E107.6.80", {"start": v(-2.44, -6.7) * mm, "end": v(-2.51, -6.67) * mm});
            skLineSegment(sketch, "E107.6.81", {"start": v(-2.58, -6.64) * mm, "end": v(-2.66, -6.61) * mm});
            skLineSegment(sketch, "E107.6.82", {"start": v(-2.51, -6.67) * mm, "end": v(-2.58, -6.64) * mm});
            skLineSegment(sketch, "E107.6.83", {"start": v(2.44, -6.7) * mm, "end": v(2.51, -6.67) * mm});
            skLineSegment(sketch, "E107.6.84", {"start": v(-2.37, -6.72) * mm, "end": v(-2.44, -6.7) * mm});
            skLineSegment(sketch, "E107.6.85", {"start": v(2.37, -6.72) * mm, "end": v(2.44, -6.7) * mm});
            skLineSegment(sketch, "E107.6.86", {"start": v(2.51, -6.67) * mm, "end": v(2.58, -6.64) * mm});
            skLineSegment(sketch, "E107.6.87", {"start": v(-0.18, -3.93) * mm, "end": v(-0.28, -3.95) * mm});
            skLineSegment(sketch, "E107.6.88", {"start": v(2.58, -6.64) * mm, "end": v(2.66, -6.61) * mm});
            skLineSegment(sketch, "E107.6.89", {"start": v(-0.28, -3.95) * mm, "end": v(-0.36, -3.97) * mm});
            skLineSegment(sketch, "E107.6.90", {"start": v(-0.06, -3.92) * mm, "end": v(-0.18, -3.93) * mm});
            skLineSegment(sketch, "E107.6.91", {"start": v(-0.03, -3.92) * mm, "end": v(-0.04, -3.92) * mm});
            skLineSegment(sketch, "E107.6.92", {"start": v(0.01, -3.92) * mm, "end": v(0.03, -3.92) * mm});
            skLineSegment(sketch, "E107.6.93", {"start": v(0.06, -3.92) * mm, "end": v(0.18, -3.93) * mm});
            skLineSegment(sketch, "E107.6.94", {"start": v(0.05, -3.92) * mm, "end": v(0.06, -3.92) * mm});
            skLineSegment(sketch, "E107.6.95", {"start": v(0.04, -3.92) * mm, "end": v(0.05, -3.92) * mm});
            skLineSegment(sketch, "E107.6.96", {"start": v(0.03, -3.92) * mm, "end": v(0.04, -3.92) * mm});
            skLineSegment(sketch, "E107.6.97", {"start": v(0, -3.92) * mm, "end": v(0.01, -3.92) * mm});
            skLineSegment(sketch, "E107.6.98", {"start": v(0, -3.92) * mm, "end": v(-0.01, -3.92) * mm});
            skLineSegment(sketch, "E107.6.99", {"start": v(-0.01, -3.92) * mm, "end": v(-0.03, -3.92) * mm});
            skLineSegment(sketch, "E107.6.100", {"start": v(-0.04, -3.92) * mm, "end": v(-0.05, -3.92) * mm});
            skLineSegment(sketch, "E107.6.101", {"start": v(-0.05, -3.92) * mm, "end": v(-0.06, -3.92) * mm});
            skPoint(sketch, "E107.7.0", {"position": v(4.03, -4.03) * mm});
            skPoint(sketch, "E107.7.1", {"position": v(4.03, -4.03) * mm});
            skLineSegment(sketch, "E107.7.2", {"start": v(2.82, -4.22) * mm, "end": v(2.9, -4.3) * mm});
            skLineSegment(sketch, "E107.7.3", {"start": v(3.23, -5.58) * mm, "end": v(3.22, -5.68) * mm});
            skLineSegment(sketch, "E107.7.4", {"start": v(3.23, -5.37) * mm, "end": v(3.23, -5.47) * mm});
            skLineSegment(sketch, "E107.7.5", {"start": v(6.1, -3.16) * mm, "end": v(6.2, -3.13) * mm});
            skLineSegment(sketch, "E107.7.6", {"start": v(4.54, -3.1) * mm, "end": v(4.63, -3.14) * mm});
            skLineSegment(sketch, "E107.7.7", {"start": v(3.2, -5.78) * mm, "end": v(3.2, -5.89) * mm});
            skLineSegment(sketch, "E107.7.8", {"start": v(3.96, -2.65) * mm, "end": v(4.05, -2.7) * mm});
            skLineSegment(sketch, "E107.7.9", {"start": v(2.56, -3.06) * mm, "end": v(2.52, -3.15) * mm});
            skLineSegment(sketch, "E107.7.10", {"start": v(3.18, -4.8) * mm, "end": v(3.2, -4.9) * mm});
            skLineSegment(sketch, "E107.7.11", {"start": v(5.37, -3.23) * mm, "end": v(5.47, -3.23) * mm});
            skLineSegment(sketch, "E107.7.12", {"start": v(6.32, -3.1) * mm, "end": v(6.43, -3.08) * mm});
            skLineSegment(sketch, "E107.7.13", {"start": v(2.49, -3.46) * mm, "end": v(2.5, -3.54) * mm});
            skLineSegment(sketch, "E107.7.14", {"start": v(4.71, -3.16) * mm, "end": v(4.8, -3.18) * mm});
            skLineSegment(sketch, "E107.7.15", {"start": v(2.7, -4.05) * mm, "end": v(2.76, -4.13) * mm});
            skLineSegment(sketch, "E107.7.16", {"start": v(2.6, -3.88) * mm, "end": v(2.65, -3.96) * mm});
            skLineSegment(sketch, "E107.7.17", {"start": v(3.1, -4.54) * mm, "end": v(3.14, -4.63) * mm});
            skLineSegment(sketch, "E107.7.18", {"start": v(2.51, -3.63) * mm, "end": v(2.54, -3.71) * mm});
            skLineSegment(sketch, "E107.7.19", {"start": v(3.1, -6.32) * mm, "end": v(3.08, -6.43) * mm});
            skLineSegment(sketch, "E107.7.20", {"start": v(2.5, -3.22) * mm, "end": v(2.5, -3.3) * mm});
            skLineSegment(sketch, "E107.7.21", {"start": v(5.58, -3.23) * mm, "end": v(5.68, -3.22) * mm});
            skLineSegment(sketch, "E107.7.22", {"start": v(4.9, -3.2) * mm, "end": v(4.99, -3.21) * mm});
            skLineSegment(sketch, "E107.7.23", {"start": v(3.16, -4.71) * mm, "end": v(3.18, -4.8) * mm});
            skLineSegment(sketch, "E107.7.24", {"start": v(2.65, -3.96) * mm, "end": v(2.7, -4.05) * mm});
            skLineSegment(sketch, "E107.7.25", {"start": v(6.2, -3.13) * mm, "end": v(6.32, -3.1) * mm});
            skLineSegment(sketch, "E107.7.26", {"start": v(3.2, -4.9) * mm, "end": v(3.21, -4.99) * mm});
            skLineSegment(sketch, "E107.7.27", {"start": v(4.63, -3.14) * mm, "end": v(4.71, -3.16) * mm});
            skLineSegment(sketch, "E107.7.28", {"start": v(4.05, -2.7) * mm, "end": v(4.13, -2.76) * mm});
            skLineSegment(sketch, "E107.7.29", {"start": v(2.9, -4.3) * mm, "end": v(2.98, -4.38) * mm});
            skLineSegment(sketch, "E107.7.30", {"start": v(3.22, -5.08) * mm, "end": v(3.23, -5.18) * mm});
            skLineSegment(sketch, "E107.7.31", {"start": v(3.22, -5.68) * mm, "end": v(3.2, -5.78) * mm});
            skLineSegment(sketch, "E107.7.32", {"start": v(2.57, -3.8) * mm, "end": v(2.6, -3.88) * mm});
            skLineSegment(sketch, "E107.7.33", {"start": v(2.52, -3.15) * mm, "end": v(2.5, -3.22) * mm});
            skLineSegment(sketch, "E107.7.34", {"start": v(2.5, -3.54) * mm, "end": v(2.51, -3.63) * mm});
            skLineSegment(sketch, "E107.7.35", {"start": v(5.47, -3.23) * mm, "end": v(5.58, -3.23) * mm});
            skLineSegment(sketch, "E107.7.36", {"start": v(4.8, -3.18) * mm, "end": v(4.9, -3.2) * mm});
            skLineSegment(sketch, "E107.7.37", {"start": v(2.5, -3.3) * mm, "end": v(2.49, -3.38) * mm});
            skLineSegment(sketch, "E107.7.38", {"start": v(5.68, -3.22) * mm, "end": v(5.78, -3.2) * mm});
            skLineSegment(sketch, "E107.7.39", {"start": v(4.99, -3.21) * mm, "end": v(5.08, -3.22) * mm});
            skLineSegment(sketch, "E107.7.40", {"start": v(3.21, -4.99) * mm, "end": v(3.22, -5.08) * mm});
            skLineSegment(sketch, "E107.7.41", {"start": v(2.8, -6.55) * mm, "end": v(2.73, -6.58) * mm});
            skLineSegment(sketch, "E107.7.42", {"start": v(3.46, -2.49) * mm, "end": v(3.54, -2.5) * mm});
            skLineSegment(sketch, "E107.7.43", {"start": v(3.54, -2.5) * mm, "end": v(3.63, -2.51) * mm});
            skLineSegment(sketch, "E107.7.44", {"start": v(3.63, -2.51) * mm, "end": v(3.71, -2.54) * mm});
            skLineSegment(sketch, "E107.7.45", {"start": v(2.9, -2.65) * mm, "end": v(2.99, -2.6) * mm});
            skLineSegment(sketch, "E107.7.46", {"start": v(2.99, -2.6) * mm, "end": v(3.06, -2.56) * mm});
            skLineSegment(sketch, "E107.7.47", {"start": v(3.06, -2.56) * mm, "end": v(3.15, -2.52) * mm});
            skLineSegment(sketch, "E107.7.48", {"start": v(3.15, -2.52) * mm, "end": v(3.22, -2.5) * mm});
            skLineSegment(sketch, "E107.7.49", {"start": v(3.22, -2.5) * mm, "end": v(3.3, -2.5) * mm});
            skLineSegment(sketch, "E107.7.50", {"start": v(3.3, -2.5) * mm, "end": v(3.38, -2.49) * mm});
            skLineSegment(sketch, "E107.7.51", {"start": v(3.38, -2.49) * mm, "end": v(3.46, -2.49) * mm});
            skLineSegment(sketch, "E107.7.52", {"start": v(3.23, -5.18) * mm, "end": v(3.23, -5.27) * mm});
            skLineSegment(sketch, "E107.7.53", {"start": v(5.78, -3.2) * mm, "end": v(5.89, -3.2) * mm});
            skLineSegment(sketch, "E107.7.54", {"start": v(3.2, -5.89) * mm, "end": v(3.18, -6) * mm});
            skLineSegment(sketch, "E107.7.55", {"start": v(2.49, -3.38) * mm, "end": v(2.49, -3.46) * mm});
            skLineSegment(sketch, "E107.7.56", {"start": v(3.71, -2.54) * mm, "end": v(3.8, -2.57) * mm});
            skLineSegment(sketch, "E107.7.57", {"start": v(3.23, -5.47) * mm, "end": v(3.23, -5.58) * mm});
            skLineSegment(sketch, "E107.7.58", {"start": v(5.08, -3.22) * mm, "end": v(5.18, -3.23) * mm});
            skLineSegment(sketch, "E107.7.59", {"start": v(5.89, -3.2) * mm, "end": v(6, -3.18) * mm});
            skLineSegment(sketch, "E107.7.60", {"start": v(4.38, -2.98) * mm, "end": v(4.47, -3.07) * mm});
            skLineSegment(sketch, "E107.7.61", {"start": v(2.98, -4.38) * mm, "end": v(3.07, -4.47) * mm});
            skLineSegment(sketch, "E107.7.62", {"start": v(3.14, -4.63) * mm, "end": v(3.16, -4.71) * mm});
            skLineSegment(sketch, "E107.7.63", {"start": v(3.8, -2.57) * mm, "end": v(3.88, -2.6) * mm});
            skLineSegment(sketch, "E107.7.64", {"start": v(2.54, -3.71) * mm, "end": v(2.57, -3.8) * mm});
            skLineSegment(sketch, "E107.7.65", {"start": v(5.18, -3.23) * mm, "end": v(5.27, -3.23) * mm});
            skLineSegment(sketch, "E107.7.66", {"start": v(3.18, -6) * mm, "end": v(3.16, -6.1) * mm});
            skLineSegment(sketch, "E107.7.67", {"start": v(6, -3.18) * mm, "end": v(6.1, -3.16) * mm});
            skLineSegment(sketch, "E107.7.68", {"start": v(4.47, -3.07) * mm, "end": v(4.54, -3.1) * mm});
            skLineSegment(sketch, "E107.7.69", {"start": v(2.76, -4.13) * mm, "end": v(2.82, -4.22) * mm});
            skLineSegment(sketch, "E107.7.70", {"start": v(3.13, -6.2) * mm, "end": v(3.1, -6.32) * mm});
            skLineSegment(sketch, "E107.7.71", {"start": v(3.88, -2.6) * mm, "end": v(3.96, -2.65) * mm});
            skLineSegment(sketch, "E107.7.72", {"start": v(3.16, -6.1) * mm, "end": v(3.13, -6.2) * mm});
            skLineSegment(sketch, "E107.7.73", {"start": v(3.23, -5.27) * mm, "end": v(3.23, -5.37) * mm});
            skLineSegment(sketch, "E107.7.74", {"start": v(5.27, -3.23) * mm, "end": v(5.37, -3.23) * mm});
            skLineSegment(sketch, "E107.7.75", {"start": v(3.07, -4.47) * mm, "end": v(3.1, -4.54) * mm});
            skLineSegment(sketch, "E107.7.76", {"start": v(4.13, -2.76) * mm, "end": v(4.22, -2.82) * mm});
            skLineSegment(sketch, "E107.7.77", {"start": v(4.22, -2.82) * mm, "end": v(4.3, -2.9) * mm});
            skLineSegment(sketch, "E107.7.78", {"start": v(4.3, -2.9) * mm, "end": v(4.38, -2.98) * mm});
            skLineSegment(sketch, "E107.7.79", {"start": v(6.55, -2.8) * mm, "end": v(6.58, -2.73) * mm});
            skLineSegment(sketch, "E107.7.80", {"start": v(3, -6.46) * mm, "end": v(2.94, -6.5) * mm});
            skLineSegment(sketch, "E107.7.81", {"start": v(2.87, -6.52) * mm, "end": v(2.8, -6.55) * mm});
            skLineSegment(sketch, "E107.7.82", {"start": v(2.94, -6.5) * mm, "end": v(2.87, -6.52) * mm});
            skLineSegment(sketch, "E107.7.83", {"start": v(6.46, -3) * mm, "end": v(6.5, -2.94) * mm});
            skLineSegment(sketch, "E107.7.84", {"start": v(3.08, -6.43) * mm, "end": v(3, -6.46) * mm});
            skLineSegment(sketch, "E107.7.85", {"start": v(6.43, -3.08) * mm, "end": v(6.46, -3) * mm});
            skLineSegment(sketch, "E107.7.86", {"start": v(6.5, -2.94) * mm, "end": v(6.52, -2.87) * mm});
            skLineSegment(sketch, "E107.7.87", {"start": v(2.65, -2.9) * mm, "end": v(2.6, -2.99) * mm});
            skLineSegment(sketch, "E107.7.88", {"start": v(6.52, -2.87) * mm, "end": v(6.55, -2.8) * mm});
            skLineSegment(sketch, "E107.7.89", {"start": v(2.6, -2.99) * mm, "end": v(2.56, -3.06) * mm});
            skLineSegment(sketch, "E107.7.90", {"start": v(2.73, -2.82) * mm, "end": v(2.65, -2.9) * mm});
            skLineSegment(sketch, "E107.7.91", {"start": v(2.75, -2.79) * mm, "end": v(2.74, -2.8) * mm});
            skLineSegment(sketch, "E107.7.92", {"start": v(2.78, -2.76) * mm, "end": v(2.79, -2.75) * mm});
            skLineSegment(sketch, "E107.7.93", {"start": v(2.82, -2.73) * mm, "end": v(2.9, -2.65) * mm});
            skLineSegment(sketch, "E107.7.94", {"start": v(2.8, -2.74) * mm, "end": v(2.82, -2.73) * mm});
            skLineSegment(sketch, "E107.7.95", {"start": v(2.8, -2.74) * mm, "end": v(2.8, -2.74) * mm});
            skLineSegment(sketch, "E107.7.96", {"start": v(2.79, -2.75) * mm, "end": v(2.8, -2.74) * mm});
            skLineSegment(sketch, "E107.7.97", {"start": v(2.77, -2.77) * mm, "end": v(2.78, -2.76) * mm});
            skLineSegment(sketch, "E107.7.98", {"start": v(2.77, -2.77) * mm, "end": v(2.76, -2.78) * mm});
            skLineSegment(sketch, "E107.7.99", {"start": v(2.76, -2.78) * mm, "end": v(2.75, -2.79) * mm});
            skLineSegment(sketch, "E107.7.100", {"start": v(2.74, -2.8) * mm, "end": v(2.74, -2.8) * mm});
            skLineSegment(sketch, "E107.7.101", {"start": v(2.74, -2.8) * mm, "end": v(2.73, -2.82) * mm});
            skCircle(sketch, "E108", {"center": v(0, 0) * mm, "radius": 1.3 * mm});
            skSolve(sketch);
        }
        {
            var Q0;
            Q0 = qSketchRegion(id + "F0", true);
            extrude(context, id + "F1", {"entities" : qUnion([Q0]), "depth" : 3 * mm});
        }
    });
